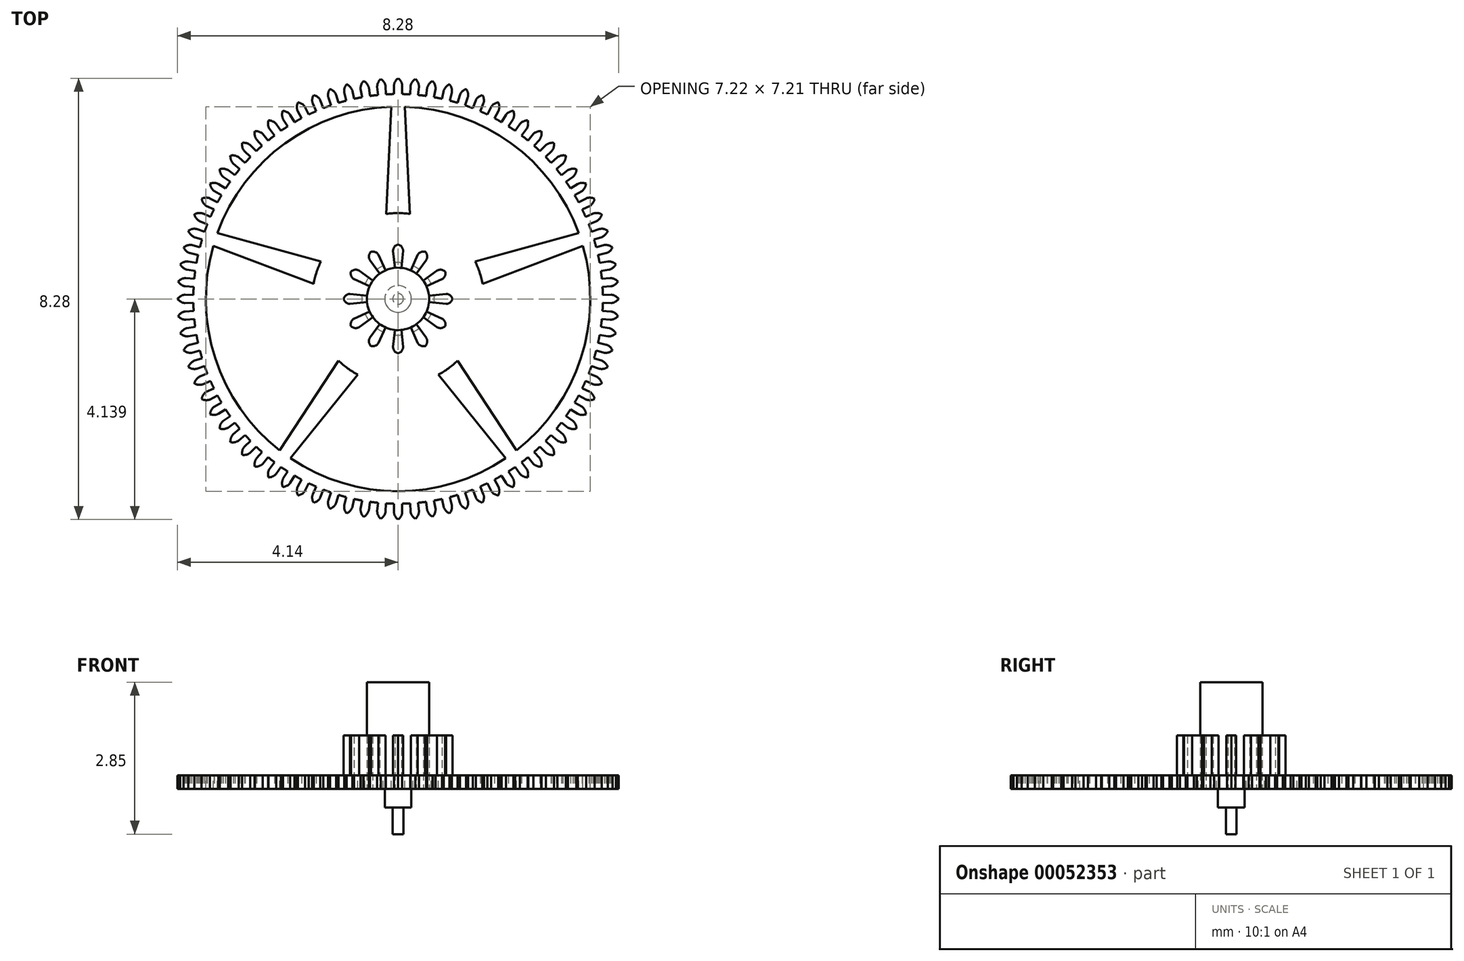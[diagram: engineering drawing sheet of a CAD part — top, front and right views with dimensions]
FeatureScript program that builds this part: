
annotation { "Feature Type Name" : "Feature", "Feature Type Description" : "" }
export const myFeature = defineFeature(function(context is Context, id is Id, definition is map)
    precondition{}
    {
        {
            var Q0;
            Q0=qCreatedBy(makeId("Top.planeOp"),FACE);
            var sketch = newSketch(context, id + "F0", { "sketchPlane" : qUnion([Q0])});
            skCircle(sketch, "E0", {"center": v(0, 0) * mm, "radius": 3.84 * mm});
            skCircle(sketch, "E1", {"center": v(0, 0) * mm, "radius": 4 * mm, "construction": true});
            skCircle(sketch, "E2", {"center": v(0, 0) * mm, "radius": 4.14 * mm, "construction": true});
            skLineSegment(sketch, "E3", {"start": v(0, 0) * mm, "end": v(0, 4) * mm, "construction": true});
            skLineSegment(sketch, "E4", {"start": v(0, 4) * mm, "end": v(0.08, 4) * mm, "construction": true});
            skLineSegment(sketch, "E5", {"start": v(0, 4) * mm, "end": v(-0.08, 4) * mm, "construction": true});
            skLineSegment(sketch, "E6", {"start": v(-0.08, 4) * mm, "end": v(0, 0) * mm, "construction": true});
            skLineSegment(sketch, "E7", {"start": v(0.08, 4) * mm, "end": v(0, 0) * mm, "construction": true});
            skLineSegment(sketch, "E8", {"start": v(-0.08, 4) * mm, "end": v(-0.08, 3.84) * mm});
            skLineSegment(sketch, "E9", {"start": v(0.08, 4) * mm, "end": v(0.08, 3.84) * mm});
            skCircle(sketch, "E10", {"center": v(-0.08, 4) * mm, "radius": 0.2 * mm, "construction": true});
            skCircle(sketch, "E11", {"center": v(0, 4.14) * mm, "radius": 0.2 * mm, "construction": true});
            skArc(sketch, "E12", {"start": v(-0.08, 4) * mm, "mid": v(-0.05, 4.08) * mm, "end": v(0, 4.14) * mm});
            skCircle(sketch, "E13", {"center": v(0.08, 4) * mm, "radius": 0.2 * mm, "construction": true});
            skArc(sketch, "E14", {"start": v(0.08, 4) * mm, "mid": v(0.05, 4.08) * mm, "end": v(0, 4.14) * mm});
            skSolve(sketch);
        }
        {
            var Q0;
            {var subQ2=sQuery(id+"F0.wireOp",EDGE,"E8");Q0=makeQuery(id+"F0.imprint","IMPRINT",FACE,{"disambiguationData":[TD([[makeQuery(id+"F0.imprint","IMPRINT",EDGE,{"derivedFrom":subQ2}),1.0]])]});}
            extrude(context, id + "F1", {"entities" : qUnion([Q0]), "depth" : 0.25 * mm});
        }
        {
            var Q0;
            Q0=makeQuery(id+"F1.opExtrude","SWEPT_BODY",BODY,{"disambiguationData":[OSD([sQuery(id+"F0.wireOp",EDGE,"E0"),sQuery(id+"F0.wireOp",EDGE,"E8"),sQuery(id+"F0.wireOp",EDGE,"E9"),sQuery(id+"F0.wireOp",EDGE,"E12"),sQuery(id+"F0.wireOp",EDGE,"E14")])]});
            var Q1;
            Q1=makeQuery(id+"F1.opExtrude","CAP_EDGE",EDGE,{"disambiguationData":[OSD([sQuery(id+"F0.wireOp",EDGE,"E0")])],"isStart":false});
            circularPattern(context, id + "F2", {"entities" : qUnion([Q0]), "axis" : qUnion([Q1]), "angle" : 4.5 * degree, "instanceCount" : round(80)});
        }
        {
            var Q0;
            {var subQ0=sQuery(id+"F0.wireOp",EDGE,"E0");var subQ2=makeQuery(id+"F0.imprint","INTERSECT",VERTEX,{"derivedFrom":[subQ0,sQuery(id+"F0.wireOp",EDGE,"E8")]});Q0=makeQuery(id+"F0.imprint","IMPRINT",FACE,{"disambiguationData":[TD([[makeQuery(id+"F0.imprint","IMPRINT",EDGE,{"disambiguationData":[TD([[subQ2,1.0]])],"derivedFrom":subQ0}),1.0]])]});}
            extrude(context, id + "F3", {"entities" : qUnion([Q0]), "depth" : 0.25 * mm});
        }
        {
            var Q0;
            Q0=makeQuery(id+"F2.opPattern","COPY",BODY,{"derivedFrom":makeQuery(id+"F1.opExtrude","SWEPT_BODY",BODY,{"disambiguationData":[OSD([sQuery(id+"F0.wireOp",EDGE,"E0"),sQuery(id+"F0.wireOp",EDGE,"E8"),sQuery(id+"F0.wireOp",EDGE,"E9"),sQuery(id+"F0.wireOp",EDGE,"E12"),sQuery(id+"F0.wireOp",EDGE,"E14")])]}),"instanceName":"94"});
            var Q1;
            Q1=makeQuery(id+"F2.opPattern","COPY",BODY,{"derivedFrom":makeQuery(id+"F1.opExtrude","SWEPT_BODY",BODY,{"disambiguationData":[OSD([sQuery(id+"F0.wireOp",EDGE,"E0"),sQuery(id+"F0.wireOp",EDGE,"E8"),sQuery(id+"F0.wireOp",EDGE,"E9"),sQuery(id+"F0.wireOp",EDGE,"E12"),sQuery(id+"F0.wireOp",EDGE,"E14")])]}),"instanceName":"73"});
            var Q2;
            Q2=makeQuery(id+"F2.opPattern","COPY",BODY,{"derivedFrom":makeQuery(id+"F1.opExtrude","SWEPT_BODY",BODY,{"disambiguationData":[OSD([sQuery(id+"F0.wireOp",EDGE,"E0"),sQuery(id+"F0.wireOp",EDGE,"E8"),sQuery(id+"F0.wireOp",EDGE,"E9"),sQuery(id+"F0.wireOp",EDGE,"E12"),sQuery(id+"F0.wireOp",EDGE,"E14")])]}),"instanceName":"71"});
            var Q3;
            Q3=makeQuery(id+"F2.opPattern","COPY",BODY,{"derivedFrom":makeQuery(id+"F1.opExtrude","SWEPT_BODY",BODY,{"disambiguationData":[OSD([sQuery(id+"F0.wireOp",EDGE,"E0"),sQuery(id+"F0.wireOp",EDGE,"E8"),sQuery(id+"F0.wireOp",EDGE,"E9"),sQuery(id+"F0.wireOp",EDGE,"E12"),sQuery(id+"F0.wireOp",EDGE,"E14")])]}),"instanceName":"78"});
            var Q4;
            Q4=makeQuery(id+"F2.opPattern","COPY",BODY,{"derivedFrom":makeQuery(id+"F1.opExtrude","SWEPT_BODY",BODY,{"disambiguationData":[OSD([sQuery(id+"F0.wireOp",EDGE,"E0"),sQuery(id+"F0.wireOp",EDGE,"E8"),sQuery(id+"F0.wireOp",EDGE,"E9"),sQuery(id+"F0.wireOp",EDGE,"E12"),sQuery(id+"F0.wireOp",EDGE,"E14")])]}),"instanceName":"82"});
            var Q5;
            Q5=makeQuery(id+"F2.opPattern","COPY",BODY,{"derivedFrom":makeQuery(id+"F1.opExtrude","SWEPT_BODY",BODY,{"disambiguationData":[OSD([sQuery(id+"F0.wireOp",EDGE,"E0"),sQuery(id+"F0.wireOp",EDGE,"E8"),sQuery(id+"F0.wireOp",EDGE,"E9"),sQuery(id+"F0.wireOp",EDGE,"E12"),sQuery(id+"F0.wireOp",EDGE,"E14")])]}),"instanceName":"90"});
            var Q6;
            Q6=makeQuery(id+"F2.opPattern","COPY",BODY,{"derivedFrom":makeQuery(id+"F1.opExtrude","SWEPT_BODY",BODY,{"disambiguationData":[OSD([sQuery(id+"F0.wireOp",EDGE,"E0"),sQuery(id+"F0.wireOp",EDGE,"E8"),sQuery(id+"F0.wireOp",EDGE,"E9"),sQuery(id+"F0.wireOp",EDGE,"E12"),sQuery(id+"F0.wireOp",EDGE,"E14")])]}),"instanceName":"77"});
            var Q7;
            Q7=makeQuery(id+"F2.opPattern","COPY",BODY,{"derivedFrom":makeQuery(id+"F1.opExtrude","SWEPT_BODY",BODY,{"disambiguationData":[OSD([sQuery(id+"F0.wireOp",EDGE,"E0"),sQuery(id+"F0.wireOp",EDGE,"E8"),sQuery(id+"F0.wireOp",EDGE,"E9"),sQuery(id+"F0.wireOp",EDGE,"E12"),sQuery(id+"F0.wireOp",EDGE,"E14")])]}),"instanceName":"76"});
            var Q8;
            Q8=makeQuery(id+"F2.opPattern","COPY",BODY,{"derivedFrom":makeQuery(id+"F1.opExtrude","SWEPT_BODY",BODY,{"disambiguationData":[OSD([sQuery(id+"F0.wireOp",EDGE,"E0"),sQuery(id+"F0.wireOp",EDGE,"E8"),sQuery(id+"F0.wireOp",EDGE,"E9"),sQuery(id+"F0.wireOp",EDGE,"E12"),sQuery(id+"F0.wireOp",EDGE,"E14")])]}),"instanceName":"84"});
            var Q9;
            Q9=makeQuery(id+"F2.opPattern","COPY",BODY,{"derivedFrom":makeQuery(id+"F1.opExtrude","SWEPT_BODY",BODY,{"disambiguationData":[OSD([sQuery(id+"F0.wireOp",EDGE,"E0"),sQuery(id+"F0.wireOp",EDGE,"E8"),sQuery(id+"F0.wireOp",EDGE,"E9"),sQuery(id+"F0.wireOp",EDGE,"E12"),sQuery(id+"F0.wireOp",EDGE,"E14")])]}),"instanceName":"80"});
            var Q10;
            Q10=makeQuery(id+"F2.opPattern","COPY",BODY,{"derivedFrom":makeQuery(id+"F1.opExtrude","SWEPT_BODY",BODY,{"disambiguationData":[OSD([sQuery(id+"F0.wireOp",EDGE,"E0"),sQuery(id+"F0.wireOp",EDGE,"E8"),sQuery(id+"F0.wireOp",EDGE,"E9"),sQuery(id+"F0.wireOp",EDGE,"E12"),sQuery(id+"F0.wireOp",EDGE,"E14")])]}),"instanceName":"37"});
            var Q11;
            Q11=makeQuery(id+"F2.opPattern","COPY",BODY,{"derivedFrom":makeQuery(id+"F1.opExtrude","SWEPT_BODY",BODY,{"disambiguationData":[OSD([sQuery(id+"F0.wireOp",EDGE,"E0"),sQuery(id+"F0.wireOp",EDGE,"E8"),sQuery(id+"F0.wireOp",EDGE,"E9"),sQuery(id+"F0.wireOp",EDGE,"E12"),sQuery(id+"F0.wireOp",EDGE,"E14")])]}),"instanceName":"44"});
            var Q12;
            Q12=makeQuery(id+"F2.opPattern","COPY",BODY,{"derivedFrom":makeQuery(id+"F1.opExtrude","SWEPT_BODY",BODY,{"disambiguationData":[OSD([sQuery(id+"F0.wireOp",EDGE,"E0"),sQuery(id+"F0.wireOp",EDGE,"E8"),sQuery(id+"F0.wireOp",EDGE,"E9"),sQuery(id+"F0.wireOp",EDGE,"E12"),sQuery(id+"F0.wireOp",EDGE,"E14")])]}),"instanceName":"88"});
            var Q13;
            Q13=makeQuery(id+"F2.opPattern","COPY",BODY,{"derivedFrom":makeQuery(id+"F1.opExtrude","SWEPT_BODY",BODY,{"disambiguationData":[OSD([sQuery(id+"F0.wireOp",EDGE,"E0"),sQuery(id+"F0.wireOp",EDGE,"E8"),sQuery(id+"F0.wireOp",EDGE,"E9"),sQuery(id+"F0.wireOp",EDGE,"E12"),sQuery(id+"F0.wireOp",EDGE,"E14")])]}),"instanceName":"60"});
            var Q14;
            Q14=makeQuery(id+"F2.opPattern","COPY",BODY,{"derivedFrom":makeQuery(id+"F1.opExtrude","SWEPT_BODY",BODY,{"disambiguationData":[OSD([sQuery(id+"F0.wireOp",EDGE,"E0"),sQuery(id+"F0.wireOp",EDGE,"E8"),sQuery(id+"F0.wireOp",EDGE,"E9"),sQuery(id+"F0.wireOp",EDGE,"E12"),sQuery(id+"F0.wireOp",EDGE,"E14")])]}),"instanceName":"69"});
            var Q15;
            Q15=makeQuery(id+"F2.opPattern","COPY",BODY,{"derivedFrom":makeQuery(id+"F1.opExtrude","SWEPT_BODY",BODY,{"disambiguationData":[OSD([sQuery(id+"F0.wireOp",EDGE,"E0"),sQuery(id+"F0.wireOp",EDGE,"E8"),sQuery(id+"F0.wireOp",EDGE,"E9"),sQuery(id+"F0.wireOp",EDGE,"E12"),sQuery(id+"F0.wireOp",EDGE,"E14")])]}),"instanceName":"12"});
            var Q16;
            Q16=makeQuery(id+"F2.opPattern","COPY",BODY,{"derivedFrom":makeQuery(id+"F1.opExtrude","SWEPT_BODY",BODY,{"disambiguationData":[OSD([sQuery(id+"F0.wireOp",EDGE,"E0"),sQuery(id+"F0.wireOp",EDGE,"E8"),sQuery(id+"F0.wireOp",EDGE,"E9"),sQuery(id+"F0.wireOp",EDGE,"E12"),sQuery(id+"F0.wireOp",EDGE,"E14")])]}),"instanceName":"28"});
            var Q17;
            Q17=makeQuery(id+"F2.opPattern","COPY",BODY,{"derivedFrom":makeQuery(id+"F1.opExtrude","SWEPT_BODY",BODY,{"disambiguationData":[OSD([sQuery(id+"F0.wireOp",EDGE,"E0"),sQuery(id+"F0.wireOp",EDGE,"E8"),sQuery(id+"F0.wireOp",EDGE,"E9"),sQuery(id+"F0.wireOp",EDGE,"E12"),sQuery(id+"F0.wireOp",EDGE,"E14")])]}),"instanceName":"92"});
            var Q18;
            Q18=makeQuery(id+"F2.opPattern","COPY",BODY,{"derivedFrom":makeQuery(id+"F1.opExtrude","SWEPT_BODY",BODY,{"disambiguationData":[OSD([sQuery(id+"F0.wireOp",EDGE,"E0"),sQuery(id+"F0.wireOp",EDGE,"E8"),sQuery(id+"F0.wireOp",EDGE,"E9"),sQuery(id+"F0.wireOp",EDGE,"E12"),sQuery(id+"F0.wireOp",EDGE,"E14")])]}),"instanceName":"89"});
            var Q19;
            Q19=makeQuery(id+"F2.opPattern","COPY",BODY,{"derivedFrom":makeQuery(id+"F1.opExtrude","SWEPT_BODY",BODY,{"disambiguationData":[OSD([sQuery(id+"F0.wireOp",EDGE,"E0"),sQuery(id+"F0.wireOp",EDGE,"E8"),sQuery(id+"F0.wireOp",EDGE,"E9"),sQuery(id+"F0.wireOp",EDGE,"E12"),sQuery(id+"F0.wireOp",EDGE,"E14")])]}),"instanceName":"7"});
            var Q20;
            Q20=makeQuery(id+"F2.opPattern","COPY",BODY,{"derivedFrom":makeQuery(id+"F1.opExtrude","SWEPT_BODY",BODY,{"disambiguationData":[OSD([sQuery(id+"F0.wireOp",EDGE,"E0"),sQuery(id+"F0.wireOp",EDGE,"E8"),sQuery(id+"F0.wireOp",EDGE,"E9"),sQuery(id+"F0.wireOp",EDGE,"E12"),sQuery(id+"F0.wireOp",EDGE,"E14")])]}),"instanceName":"14"});
            var Q21;
            Q21=makeQuery(id+"F2.opPattern","COPY",BODY,{"derivedFrom":makeQuery(id+"F1.opExtrude","SWEPT_BODY",BODY,{"disambiguationData":[OSD([sQuery(id+"F0.wireOp",EDGE,"E0"),sQuery(id+"F0.wireOp",EDGE,"E8"),sQuery(id+"F0.wireOp",EDGE,"E9"),sQuery(id+"F0.wireOp",EDGE,"E12"),sQuery(id+"F0.wireOp",EDGE,"E14")])]}),"instanceName":"32"});
            var Q22;
            Q22=makeQuery(id+"F2.opPattern","COPY",BODY,{"derivedFrom":makeQuery(id+"F1.opExtrude","SWEPT_BODY",BODY,{"disambiguationData":[OSD([sQuery(id+"F0.wireOp",EDGE,"E0"),sQuery(id+"F0.wireOp",EDGE,"E8"),sQuery(id+"F0.wireOp",EDGE,"E9"),sQuery(id+"F0.wireOp",EDGE,"E12"),sQuery(id+"F0.wireOp",EDGE,"E14")])]}),"instanceName":"25"});
            var Q23;
            Q23=makeQuery(id+"F2.opPattern","COPY",BODY,{"derivedFrom":makeQuery(id+"F1.opExtrude","SWEPT_BODY",BODY,{"disambiguationData":[OSD([sQuery(id+"F0.wireOp",EDGE,"E0"),sQuery(id+"F0.wireOp",EDGE,"E8"),sQuery(id+"F0.wireOp",EDGE,"E9"),sQuery(id+"F0.wireOp",EDGE,"E12"),sQuery(id+"F0.wireOp",EDGE,"E14")])]}),"instanceName":"34"});
            var Q24;
            Q24=makeQuery(id+"F2.opPattern","COPY",BODY,{"derivedFrom":makeQuery(id+"F1.opExtrude","SWEPT_BODY",BODY,{"disambiguationData":[OSD([sQuery(id+"F0.wireOp",EDGE,"E0"),sQuery(id+"F0.wireOp",EDGE,"E8"),sQuery(id+"F0.wireOp",EDGE,"E9"),sQuery(id+"F0.wireOp",EDGE,"E12"),sQuery(id+"F0.wireOp",EDGE,"E14")])]}),"instanceName":"30"});
            var Q25;
            Q25=makeQuery(id+"F2.opPattern","COPY",BODY,{"derivedFrom":makeQuery(id+"F1.opExtrude","SWEPT_BODY",BODY,{"disambiguationData":[OSD([sQuery(id+"F0.wireOp",EDGE,"E0"),sQuery(id+"F0.wireOp",EDGE,"E8"),sQuery(id+"F0.wireOp",EDGE,"E9"),sQuery(id+"F0.wireOp",EDGE,"E12"),sQuery(id+"F0.wireOp",EDGE,"E14")])]}),"instanceName":"66"});
            var Q26;
            Q26=makeQuery(id+"F2.opPattern","COPY",BODY,{"derivedFrom":makeQuery(id+"F1.opExtrude","SWEPT_BODY",BODY,{"disambiguationData":[OSD([sQuery(id+"F0.wireOp",EDGE,"E0"),sQuery(id+"F0.wireOp",EDGE,"E8"),sQuery(id+"F0.wireOp",EDGE,"E9"),sQuery(id+"F0.wireOp",EDGE,"E12"),sQuery(id+"F0.wireOp",EDGE,"E14")])]}),"instanceName":"18"});
            var Q27;
            Q27=makeQuery(id+"F2.opPattern","COPY",BODY,{"derivedFrom":makeQuery(id+"F1.opExtrude","SWEPT_BODY",BODY,{"disambiguationData":[OSD([sQuery(id+"F0.wireOp",EDGE,"E0"),sQuery(id+"F0.wireOp",EDGE,"E8"),sQuery(id+"F0.wireOp",EDGE,"E9"),sQuery(id+"F0.wireOp",EDGE,"E12"),sQuery(id+"F0.wireOp",EDGE,"E14")])]}),"instanceName":"59"});
            var Q28;
            Q28=makeQuery(id+"F2.opPattern","COPY",BODY,{"derivedFrom":makeQuery(id+"F1.opExtrude","SWEPT_BODY",BODY,{"disambiguationData":[OSD([sQuery(id+"F0.wireOp",EDGE,"E0"),sQuery(id+"F0.wireOp",EDGE,"E8"),sQuery(id+"F0.wireOp",EDGE,"E9"),sQuery(id+"F0.wireOp",EDGE,"E12"),sQuery(id+"F0.wireOp",EDGE,"E14")])]}),"instanceName":"50"});
            var Q29;
            Q29=makeQuery(id+"F2.opPattern","COPY",BODY,{"derivedFrom":makeQuery(id+"F1.opExtrude","SWEPT_BODY",BODY,{"disambiguationData":[OSD([sQuery(id+"F0.wireOp",EDGE,"E0"),sQuery(id+"F0.wireOp",EDGE,"E8"),sQuery(id+"F0.wireOp",EDGE,"E9"),sQuery(id+"F0.wireOp",EDGE,"E12"),sQuery(id+"F0.wireOp",EDGE,"E14")])]}),"instanceName":"46"});
            var Q30;
            Q30=makeQuery(id+"F2.opPattern","COPY",BODY,{"derivedFrom":makeQuery(id+"F1.opExtrude","SWEPT_BODY",BODY,{"disambiguationData":[OSD([sQuery(id+"F0.wireOp",EDGE,"E0"),sQuery(id+"F0.wireOp",EDGE,"E8"),sQuery(id+"F0.wireOp",EDGE,"E9"),sQuery(id+"F0.wireOp",EDGE,"E12"),sQuery(id+"F0.wireOp",EDGE,"E14")])]}),"instanceName":"57"});
            var Q31;
            Q31=makeQuery(id+"F2.opPattern","COPY",BODY,{"derivedFrom":makeQuery(id+"F1.opExtrude","SWEPT_BODY",BODY,{"disambiguationData":[OSD([sQuery(id+"F0.wireOp",EDGE,"E0"),sQuery(id+"F0.wireOp",EDGE,"E8"),sQuery(id+"F0.wireOp",EDGE,"E9"),sQuery(id+"F0.wireOp",EDGE,"E12"),sQuery(id+"F0.wireOp",EDGE,"E14")])]}),"instanceName":"64"});
            var Q32;
            Q32=makeQuery(id+"F2.opPattern","COPY",BODY,{"derivedFrom":makeQuery(id+"F1.opExtrude","SWEPT_BODY",BODY,{"disambiguationData":[OSD([sQuery(id+"F0.wireOp",EDGE,"E0"),sQuery(id+"F0.wireOp",EDGE,"E8"),sQuery(id+"F0.wireOp",EDGE,"E9"),sQuery(id+"F0.wireOp",EDGE,"E12"),sQuery(id+"F0.wireOp",EDGE,"E14")])]}),"instanceName":"62"});
            var Q33;
            Q33=makeQuery(id+"F2.opPattern","COPY",BODY,{"derivedFrom":makeQuery(id+"F1.opExtrude","SWEPT_BODY",BODY,{"disambiguationData":[OSD([sQuery(id+"F0.wireOp",EDGE,"E0"),sQuery(id+"F0.wireOp",EDGE,"E8"),sQuery(id+"F0.wireOp",EDGE,"E9"),sQuery(id+"F0.wireOp",EDGE,"E12"),sQuery(id+"F0.wireOp",EDGE,"E14")])]}),"instanceName":"5"});
            var Q34;
            Q34=makeQuery(id+"F2.opPattern","COPY",BODY,{"derivedFrom":makeQuery(id+"F1.opExtrude","SWEPT_BODY",BODY,{"disambiguationData":[OSD([sQuery(id+"F0.wireOp",EDGE,"E0"),sQuery(id+"F0.wireOp",EDGE,"E8"),sQuery(id+"F0.wireOp",EDGE,"E9"),sQuery(id+"F0.wireOp",EDGE,"E12"),sQuery(id+"F0.wireOp",EDGE,"E14")])]}),"instanceName":"16"});
            var Q35;
            Q35=makeQuery(id+"F2.opPattern","COPY",BODY,{"derivedFrom":makeQuery(id+"F1.opExtrude","SWEPT_BODY",BODY,{"disambiguationData":[OSD([sQuery(id+"F0.wireOp",EDGE,"E0"),sQuery(id+"F0.wireOp",EDGE,"E8"),sQuery(id+"F0.wireOp",EDGE,"E9"),sQuery(id+"F0.wireOp",EDGE,"E12"),sQuery(id+"F0.wireOp",EDGE,"E14")])]}),"instanceName":"31"});
            var Q36;
            Q36=makeQuery(id+"F2.opPattern","COPY",BODY,{"derivedFrom":makeQuery(id+"F1.opExtrude","SWEPT_BODY",BODY,{"disambiguationData":[OSD([sQuery(id+"F0.wireOp",EDGE,"E0"),sQuery(id+"F0.wireOp",EDGE,"E8"),sQuery(id+"F0.wireOp",EDGE,"E9"),sQuery(id+"F0.wireOp",EDGE,"E12"),sQuery(id+"F0.wireOp",EDGE,"E14")])]}),"instanceName":"21"});
            var Q37;
            Q37=makeQuery(id+"F2.opPattern","COPY",BODY,{"derivedFrom":makeQuery(id+"F1.opExtrude","SWEPT_BODY",BODY,{"disambiguationData":[OSD([sQuery(id+"F0.wireOp",EDGE,"E0"),sQuery(id+"F0.wireOp",EDGE,"E8"),sQuery(id+"F0.wireOp",EDGE,"E9"),sQuery(id+"F0.wireOp",EDGE,"E12"),sQuery(id+"F0.wireOp",EDGE,"E14")])]}),"instanceName":"43"});
            var Q38;
            Q38=makeQuery(id+"F2.opPattern","COPY",BODY,{"derivedFrom":makeQuery(id+"F1.opExtrude","SWEPT_BODY",BODY,{"disambiguationData":[OSD([sQuery(id+"F0.wireOp",EDGE,"E0"),sQuery(id+"F0.wireOp",EDGE,"E8"),sQuery(id+"F0.wireOp",EDGE,"E9"),sQuery(id+"F0.wireOp",EDGE,"E12"),sQuery(id+"F0.wireOp",EDGE,"E14")])]}),"instanceName":"53"});
            var Q39;
            Q39=makeQuery(id+"F2.opPattern","COPY",BODY,{"derivedFrom":makeQuery(id+"F1.opExtrude","SWEPT_BODY",BODY,{"disambiguationData":[OSD([sQuery(id+"F0.wireOp",EDGE,"E0"),sQuery(id+"F0.wireOp",EDGE,"E8"),sQuery(id+"F0.wireOp",EDGE,"E9"),sQuery(id+"F0.wireOp",EDGE,"E12"),sQuery(id+"F0.wireOp",EDGE,"E14")])]}),"instanceName":"49"});
            var Q40;
            Q40=makeQuery(id+"F2.opPattern","COPY",BODY,{"derivedFrom":makeQuery(id+"F1.opExtrude","SWEPT_BODY",BODY,{"disambiguationData":[OSD([sQuery(id+"F0.wireOp",EDGE,"E0"),sQuery(id+"F0.wireOp",EDGE,"E8"),sQuery(id+"F0.wireOp",EDGE,"E9"),sQuery(id+"F0.wireOp",EDGE,"E12"),sQuery(id+"F0.wireOp",EDGE,"E14")])]}),"instanceName":"65"});
            var Q41;
            Q41=makeQuery(id+"F2.opPattern","COPY",BODY,{"derivedFrom":makeQuery(id+"F1.opExtrude","SWEPT_BODY",BODY,{"disambiguationData":[OSD([sQuery(id+"F0.wireOp",EDGE,"E0"),sQuery(id+"F0.wireOp",EDGE,"E8"),sQuery(id+"F0.wireOp",EDGE,"E9"),sQuery(id+"F0.wireOp",EDGE,"E12"),sQuery(id+"F0.wireOp",EDGE,"E14")])]}),"instanceName":"74"});
            var Q42;
            Q42=makeQuery(id+"F2.opPattern","COPY",BODY,{"derivedFrom":makeQuery(id+"F1.opExtrude","SWEPT_BODY",BODY,{"disambiguationData":[OSD([sQuery(id+"F0.wireOp",EDGE,"E0"),sQuery(id+"F0.wireOp",EDGE,"E8"),sQuery(id+"F0.wireOp",EDGE,"E9"),sQuery(id+"F0.wireOp",EDGE,"E12"),sQuery(id+"F0.wireOp",EDGE,"E14")])]}),"instanceName":"17"});
            var Q43;
            Q43=makeQuery(id+"F2.opPattern","COPY",BODY,{"derivedFrom":makeQuery(id+"F1.opExtrude","SWEPT_BODY",BODY,{"disambiguationData":[OSD([sQuery(id+"F0.wireOp",EDGE,"E0"),sQuery(id+"F0.wireOp",EDGE,"E8"),sQuery(id+"F0.wireOp",EDGE,"E9"),sQuery(id+"F0.wireOp",EDGE,"E12"),sQuery(id+"F0.wireOp",EDGE,"E14")])]}),"instanceName":"58"});
            var Q44;
            Q44=makeQuery(id+"F2.opPattern","COPY",BODY,{"derivedFrom":makeQuery(id+"F1.opExtrude","SWEPT_BODY",BODY,{"disambiguationData":[OSD([sQuery(id+"F0.wireOp",EDGE,"E0"),sQuery(id+"F0.wireOp",EDGE,"E8"),sQuery(id+"F0.wireOp",EDGE,"E9"),sQuery(id+"F0.wireOp",EDGE,"E12"),sQuery(id+"F0.wireOp",EDGE,"E14")])]}),"instanceName":"85"});
            var Q45;
            Q45=makeQuery(id+"F2.opPattern","COPY",BODY,{"derivedFrom":makeQuery(id+"F1.opExtrude","SWEPT_BODY",BODY,{"disambiguationData":[OSD([sQuery(id+"F0.wireOp",EDGE,"E0"),sQuery(id+"F0.wireOp",EDGE,"E8"),sQuery(id+"F0.wireOp",EDGE,"E9"),sQuery(id+"F0.wireOp",EDGE,"E12"),sQuery(id+"F0.wireOp",EDGE,"E14")])]}),"instanceName":"81"});
            var Q46;
            Q46=makeQuery(id+"F2.opPattern","COPY",BODY,{"derivedFrom":makeQuery(id+"F1.opExtrude","SWEPT_BODY",BODY,{"disambiguationData":[OSD([sQuery(id+"F0.wireOp",EDGE,"E0"),sQuery(id+"F0.wireOp",EDGE,"E8"),sQuery(id+"F0.wireOp",EDGE,"E9"),sQuery(id+"F0.wireOp",EDGE,"E12"),sQuery(id+"F0.wireOp",EDGE,"E14")])]}),"instanceName":"42"});
            var Q47;
            Q47=makeQuery(id+"F2.opPattern","COPY",BODY,{"derivedFrom":makeQuery(id+"F1.opExtrude","SWEPT_BODY",BODY,{"disambiguationData":[OSD([sQuery(id+"F0.wireOp",EDGE,"E0"),sQuery(id+"F0.wireOp",EDGE,"E8"),sQuery(id+"F0.wireOp",EDGE,"E9"),sQuery(id+"F0.wireOp",EDGE,"E12"),sQuery(id+"F0.wireOp",EDGE,"E14")])]}),"instanceName":"10"});
            var Q48;
            Q48=makeQuery(id+"F2.opPattern","COPY",BODY,{"derivedFrom":makeQuery(id+"F1.opExtrude","SWEPT_BODY",BODY,{"disambiguationData":[OSD([sQuery(id+"F0.wireOp",EDGE,"E0"),sQuery(id+"F0.wireOp",EDGE,"E8"),sQuery(id+"F0.wireOp",EDGE,"E9"),sQuery(id+"F0.wireOp",EDGE,"E12"),sQuery(id+"F0.wireOp",EDGE,"E14")])]}),"instanceName":"79"});
            var Q49;
            Q49=makeQuery(id+"F2.opPattern","COPY",BODY,{"derivedFrom":makeQuery(id+"F1.opExtrude","SWEPT_BODY",BODY,{"disambiguationData":[OSD([sQuery(id+"F0.wireOp",EDGE,"E0"),sQuery(id+"F0.wireOp",EDGE,"E8"),sQuery(id+"F0.wireOp",EDGE,"E9"),sQuery(id+"F0.wireOp",EDGE,"E12"),sQuery(id+"F0.wireOp",EDGE,"E14")])]}),"instanceName":"83"});
            var Q50;
            Q50=makeQuery(id+"F2.opPattern","COPY",BODY,{"derivedFrom":makeQuery(id+"F1.opExtrude","SWEPT_BODY",BODY,{"disambiguationData":[OSD([sQuery(id+"F0.wireOp",EDGE,"E0"),sQuery(id+"F0.wireOp",EDGE,"E8"),sQuery(id+"F0.wireOp",EDGE,"E9"),sQuery(id+"F0.wireOp",EDGE,"E12"),sQuery(id+"F0.wireOp",EDGE,"E14")])]}),"instanceName":"13"});
            var Q51;
            Q51=makeQuery(id+"F2.opPattern","COPY",BODY,{"derivedFrom":makeQuery(id+"F1.opExtrude","SWEPT_BODY",BODY,{"disambiguationData":[OSD([sQuery(id+"F0.wireOp",EDGE,"E0"),sQuery(id+"F0.wireOp",EDGE,"E8"),sQuery(id+"F0.wireOp",EDGE,"E9"),sQuery(id+"F0.wireOp",EDGE,"E12"),sQuery(id+"F0.wireOp",EDGE,"E14")])]}),"instanceName":"86"});
            var Q52;
            Q52=makeQuery(id+"F2.opPattern","COPY",BODY,{"derivedFrom":makeQuery(id+"F1.opExtrude","SWEPT_BODY",BODY,{"disambiguationData":[OSD([sQuery(id+"F0.wireOp",EDGE,"E0"),sQuery(id+"F0.wireOp",EDGE,"E8"),sQuery(id+"F0.wireOp",EDGE,"E9"),sQuery(id+"F0.wireOp",EDGE,"E12"),sQuery(id+"F0.wireOp",EDGE,"E14")])]}),"instanceName":"3"});
            var Q53;
            Q53=makeQuery(id+"F2.opPattern","COPY",BODY,{"derivedFrom":makeQuery(id+"F1.opExtrude","SWEPT_BODY",BODY,{"disambiguationData":[OSD([sQuery(id+"F0.wireOp",EDGE,"E0"),sQuery(id+"F0.wireOp",EDGE,"E8"),sQuery(id+"F0.wireOp",EDGE,"E9"),sQuery(id+"F0.wireOp",EDGE,"E12"),sQuery(id+"F0.wireOp",EDGE,"E14")])]}),"instanceName":"70"});
            var Q54;
            Q54=makeQuery(id+"F2.opPattern","COPY",BODY,{"derivedFrom":makeQuery(id+"F1.opExtrude","SWEPT_BODY",BODY,{"disambiguationData":[OSD([sQuery(id+"F0.wireOp",EDGE,"E0"),sQuery(id+"F0.wireOp",EDGE,"E8"),sQuery(id+"F0.wireOp",EDGE,"E9"),sQuery(id+"F0.wireOp",EDGE,"E12"),sQuery(id+"F0.wireOp",EDGE,"E14")])]}),"instanceName":"61"});
            var Q55;
            Q55=makeQuery(id+"F2.opPattern","COPY",BODY,{"derivedFrom":makeQuery(id+"F1.opExtrude","SWEPT_BODY",BODY,{"disambiguationData":[OSD([sQuery(id+"F0.wireOp",EDGE,"E0"),sQuery(id+"F0.wireOp",EDGE,"E8"),sQuery(id+"F0.wireOp",EDGE,"E9"),sQuery(id+"F0.wireOp",EDGE,"E12"),sQuery(id+"F0.wireOp",EDGE,"E14")])]}),"instanceName":"87"});
            var Q56;
            Q56=makeQuery(id+"F2.opPattern","COPY",BODY,{"derivedFrom":makeQuery(id+"F1.opExtrude","SWEPT_BODY",BODY,{"disambiguationData":[OSD([sQuery(id+"F0.wireOp",EDGE,"E0"),sQuery(id+"F0.wireOp",EDGE,"E8"),sQuery(id+"F0.wireOp",EDGE,"E9"),sQuery(id+"F0.wireOp",EDGE,"E12"),sQuery(id+"F0.wireOp",EDGE,"E14")])]}),"instanceName":"35"});
            var Q57;
            Q57=makeQuery(id+"F2.opPattern","COPY",BODY,{"derivedFrom":makeQuery(id+"F1.opExtrude","SWEPT_BODY",BODY,{"disambiguationData":[OSD([sQuery(id+"F0.wireOp",EDGE,"E0"),sQuery(id+"F0.wireOp",EDGE,"E8"),sQuery(id+"F0.wireOp",EDGE,"E9"),sQuery(id+"F0.wireOp",EDGE,"E12"),sQuery(id+"F0.wireOp",EDGE,"E14")])]}),"instanceName":"47"});
            var Q58;
            Q58=makeQuery(id+"F2.opPattern","COPY",BODY,{"derivedFrom":makeQuery(id+"F1.opExtrude","SWEPT_BODY",BODY,{"disambiguationData":[OSD([sQuery(id+"F0.wireOp",EDGE,"E0"),sQuery(id+"F0.wireOp",EDGE,"E8"),sQuery(id+"F0.wireOp",EDGE,"E9"),sQuery(id+"F0.wireOp",EDGE,"E12"),sQuery(id+"F0.wireOp",EDGE,"E14")])]}),"instanceName":"39"});
            var Q59;
            Q59=makeQuery(id+"F2.opPattern","COPY",BODY,{"derivedFrom":makeQuery(id+"F1.opExtrude","SWEPT_BODY",BODY,{"disambiguationData":[OSD([sQuery(id+"F0.wireOp",EDGE,"E0"),sQuery(id+"F0.wireOp",EDGE,"E8"),sQuery(id+"F0.wireOp",EDGE,"E9"),sQuery(id+"F0.wireOp",EDGE,"E12"),sQuery(id+"F0.wireOp",EDGE,"E14")])]}),"instanceName":"51"});
            var Q60;
            Q60=makeQuery(id+"F2.opPattern","COPY",BODY,{"derivedFrom":makeQuery(id+"F1.opExtrude","SWEPT_BODY",BODY,{"disambiguationData":[OSD([sQuery(id+"F0.wireOp",EDGE,"E0"),sQuery(id+"F0.wireOp",EDGE,"E8"),sQuery(id+"F0.wireOp",EDGE,"E9"),sQuery(id+"F0.wireOp",EDGE,"E12"),sQuery(id+"F0.wireOp",EDGE,"E14")])]}),"instanceName":"67"});
            var Q61;
            Q61=makeQuery(id+"F2.opPattern","COPY",BODY,{"derivedFrom":makeQuery(id+"F1.opExtrude","SWEPT_BODY",BODY,{"disambiguationData":[OSD([sQuery(id+"F0.wireOp",EDGE,"E0"),sQuery(id+"F0.wireOp",EDGE,"E8"),sQuery(id+"F0.wireOp",EDGE,"E9"),sQuery(id+"F0.wireOp",EDGE,"E12"),sQuery(id+"F0.wireOp",EDGE,"E14")])]}),"instanceName":"26"});
            var Q62;
            Q62=makeQuery(id+"F2.opPattern","COPY",BODY,{"derivedFrom":makeQuery(id+"F1.opExtrude","SWEPT_BODY",BODY,{"disambiguationData":[OSD([sQuery(id+"F0.wireOp",EDGE,"E0"),sQuery(id+"F0.wireOp",EDGE,"E8"),sQuery(id+"F0.wireOp",EDGE,"E9"),sQuery(id+"F0.wireOp",EDGE,"E12"),sQuery(id+"F0.wireOp",EDGE,"E14")])]}),"instanceName":"19"});
            var Q63;
            Q63=makeQuery(id+"F2.opPattern","COPY",BODY,{"derivedFrom":makeQuery(id+"F1.opExtrude","SWEPT_BODY",BODY,{"disambiguationData":[OSD([sQuery(id+"F0.wireOp",EDGE,"E0"),sQuery(id+"F0.wireOp",EDGE,"E8"),sQuery(id+"F0.wireOp",EDGE,"E9"),sQuery(id+"F0.wireOp",EDGE,"E12"),sQuery(id+"F0.wireOp",EDGE,"E14")])]}),"instanceName":"23"});
            var Q64;
            Q64=makeQuery(id+"F2.opPattern","COPY",BODY,{"derivedFrom":makeQuery(id+"F1.opExtrude","SWEPT_BODY",BODY,{"disambiguationData":[OSD([sQuery(id+"F0.wireOp",EDGE,"E0"),sQuery(id+"F0.wireOp",EDGE,"E8"),sQuery(id+"F0.wireOp",EDGE,"E9"),sQuery(id+"F0.wireOp",EDGE,"E12"),sQuery(id+"F0.wireOp",EDGE,"E14")])]}),"instanceName":"27"});
            var Q65;
            Q65=makeQuery(id+"F2.opPattern","COPY",BODY,{"derivedFrom":makeQuery(id+"F1.opExtrude","SWEPT_BODY",BODY,{"disambiguationData":[OSD([sQuery(id+"F0.wireOp",EDGE,"E0"),sQuery(id+"F0.wireOp",EDGE,"E8"),sQuery(id+"F0.wireOp",EDGE,"E9"),sQuery(id+"F0.wireOp",EDGE,"E12"),sQuery(id+"F0.wireOp",EDGE,"E14")])]}),"instanceName":"29"});
            var Q66;
            Q66=makeQuery(id+"F2.opPattern","COPY",BODY,{"derivedFrom":makeQuery(id+"F1.opExtrude","SWEPT_BODY",BODY,{"disambiguationData":[OSD([sQuery(id+"F0.wireOp",EDGE,"E0"),sQuery(id+"F0.wireOp",EDGE,"E8"),sQuery(id+"F0.wireOp",EDGE,"E9"),sQuery(id+"F0.wireOp",EDGE,"E12"),sQuery(id+"F0.wireOp",EDGE,"E14")])]}),"instanceName":"11"});
            var Q67;
            Q67=makeQuery(id+"F2.opPattern","COPY",BODY,{"derivedFrom":makeQuery(id+"F1.opExtrude","SWEPT_BODY",BODY,{"disambiguationData":[OSD([sQuery(id+"F0.wireOp",EDGE,"E0"),sQuery(id+"F0.wireOp",EDGE,"E8"),sQuery(id+"F0.wireOp",EDGE,"E9"),sQuery(id+"F0.wireOp",EDGE,"E12"),sQuery(id+"F0.wireOp",EDGE,"E14")])]}),"instanceName":"33"});
            var Q68;
            Q68=makeQuery(id+"F2.opPattern","COPY",BODY,{"derivedFrom":makeQuery(id+"F1.opExtrude","SWEPT_BODY",BODY,{"disambiguationData":[OSD([sQuery(id+"F0.wireOp",EDGE,"E0"),sQuery(id+"F0.wireOp",EDGE,"E8"),sQuery(id+"F0.wireOp",EDGE,"E9"),sQuery(id+"F0.wireOp",EDGE,"E12"),sQuery(id+"F0.wireOp",EDGE,"E14")])]}),"instanceName":"41"});
            var Q69;
            Q69=makeQuery(id+"F2.opPattern","COPY",BODY,{"derivedFrom":makeQuery(id+"F1.opExtrude","SWEPT_BODY",BODY,{"disambiguationData":[OSD([sQuery(id+"F0.wireOp",EDGE,"E0"),sQuery(id+"F0.wireOp",EDGE,"E8"),sQuery(id+"F0.wireOp",EDGE,"E9"),sQuery(id+"F0.wireOp",EDGE,"E12"),sQuery(id+"F0.wireOp",EDGE,"E14")])]}),"instanceName":"24"});
            var Q70;
            Q70=makeQuery(id+"F2.opPattern","COPY",BODY,{"derivedFrom":makeQuery(id+"F1.opExtrude","SWEPT_BODY",BODY,{"disambiguationData":[OSD([sQuery(id+"F0.wireOp",EDGE,"E0"),sQuery(id+"F0.wireOp",EDGE,"E8"),sQuery(id+"F0.wireOp",EDGE,"E9"),sQuery(id+"F0.wireOp",EDGE,"E12"),sQuery(id+"F0.wireOp",EDGE,"E14")])]}),"instanceName":"22"});
            var Q71;
            Q71=makeQuery(id+"F2.opPattern","COPY",BODY,{"derivedFrom":makeQuery(id+"F1.opExtrude","SWEPT_BODY",BODY,{"disambiguationData":[OSD([sQuery(id+"F0.wireOp",EDGE,"E0"),sQuery(id+"F0.wireOp",EDGE,"E8"),sQuery(id+"F0.wireOp",EDGE,"E9"),sQuery(id+"F0.wireOp",EDGE,"E12"),sQuery(id+"F0.wireOp",EDGE,"E14")])]}),"instanceName":"8"});
            var Q72;
            Q72=makeQuery(id+"F2.opPattern","COPY",BODY,{"derivedFrom":makeQuery(id+"F1.opExtrude","SWEPT_BODY",BODY,{"disambiguationData":[OSD([sQuery(id+"F0.wireOp",EDGE,"E0"),sQuery(id+"F0.wireOp",EDGE,"E8"),sQuery(id+"F0.wireOp",EDGE,"E9"),sQuery(id+"F0.wireOp",EDGE,"E12"),sQuery(id+"F0.wireOp",EDGE,"E14")])]}),"instanceName":"40"});
            var Q73;
            Q73=makeQuery(id+"F2.opPattern","COPY",BODY,{"derivedFrom":makeQuery(id+"F1.opExtrude","SWEPT_BODY",BODY,{"disambiguationData":[OSD([sQuery(id+"F0.wireOp",EDGE,"E0"),sQuery(id+"F0.wireOp",EDGE,"E8"),sQuery(id+"F0.wireOp",EDGE,"E9"),sQuery(id+"F0.wireOp",EDGE,"E12"),sQuery(id+"F0.wireOp",EDGE,"E14")])]}),"instanceName":"54"});
            var Q74;
            Q74=makeQuery(id+"F2.opPattern","COPY",BODY,{"derivedFrom":makeQuery(id+"F1.opExtrude","SWEPT_BODY",BODY,{"disambiguationData":[OSD([sQuery(id+"F0.wireOp",EDGE,"E0"),sQuery(id+"F0.wireOp",EDGE,"E8"),sQuery(id+"F0.wireOp",EDGE,"E9"),sQuery(id+"F0.wireOp",EDGE,"E12"),sQuery(id+"F0.wireOp",EDGE,"E14")])]}),"instanceName":"56"});
            var Q75;
            Q75=makeQuery(id+"F2.opPattern","COPY",BODY,{"derivedFrom":makeQuery(id+"F1.opExtrude","SWEPT_BODY",BODY,{"disambiguationData":[OSD([sQuery(id+"F0.wireOp",EDGE,"E0"),sQuery(id+"F0.wireOp",EDGE,"E8"),sQuery(id+"F0.wireOp",EDGE,"E9"),sQuery(id+"F0.wireOp",EDGE,"E12"),sQuery(id+"F0.wireOp",EDGE,"E14")])]}),"instanceName":"72"});
            var Q76;
            Q76=makeQuery(id+"F2.opPattern","COPY",BODY,{"derivedFrom":makeQuery(id+"F1.opExtrude","SWEPT_BODY",BODY,{"disambiguationData":[OSD([sQuery(id+"F0.wireOp",EDGE,"E0"),sQuery(id+"F0.wireOp",EDGE,"E8"),sQuery(id+"F0.wireOp",EDGE,"E9"),sQuery(id+"F0.wireOp",EDGE,"E12"),sQuery(id+"F0.wireOp",EDGE,"E14")])]}),"instanceName":"15"});
            var Q77;
            Q77=makeQuery(id+"F2.opPattern","COPY",BODY,{"derivedFrom":makeQuery(id+"F1.opExtrude","SWEPT_BODY",BODY,{"disambiguationData":[OSD([sQuery(id+"F0.wireOp",EDGE,"E0"),sQuery(id+"F0.wireOp",EDGE,"E8"),sQuery(id+"F0.wireOp",EDGE,"E9"),sQuery(id+"F0.wireOp",EDGE,"E12"),sQuery(id+"F0.wireOp",EDGE,"E14")])]}),"instanceName":"63"});
            var Q78;
            Q78=makeQuery(id+"F2.opPattern","COPY",BODY,{"derivedFrom":makeQuery(id+"F1.opExtrude","SWEPT_BODY",BODY,{"disambiguationData":[OSD([sQuery(id+"F0.wireOp",EDGE,"E0"),sQuery(id+"F0.wireOp",EDGE,"E8"),sQuery(id+"F0.wireOp",EDGE,"E9"),sQuery(id+"F0.wireOp",EDGE,"E12"),sQuery(id+"F0.wireOp",EDGE,"E14")])]}),"instanceName":"95"});
            var Q79;
            Q79=makeQuery(id+"F2.opPattern","COPY",BODY,{"derivedFrom":makeQuery(id+"F1.opExtrude","SWEPT_BODY",BODY,{"disambiguationData":[OSD([sQuery(id+"F0.wireOp",EDGE,"E0"),sQuery(id+"F0.wireOp",EDGE,"E8"),sQuery(id+"F0.wireOp",EDGE,"E9"),sQuery(id+"F0.wireOp",EDGE,"E12"),sQuery(id+"F0.wireOp",EDGE,"E14")])]}),"instanceName":"6"});
            var Q80;
            Q80=makeQuery(id+"F2.opPattern","COPY",BODY,{"derivedFrom":makeQuery(id+"F1.opExtrude","SWEPT_BODY",BODY,{"disambiguationData":[OSD([sQuery(id+"F0.wireOp",EDGE,"E0"),sQuery(id+"F0.wireOp",EDGE,"E8"),sQuery(id+"F0.wireOp",EDGE,"E9"),sQuery(id+"F0.wireOp",EDGE,"E12"),sQuery(id+"F0.wireOp",EDGE,"E14")])]}),"instanceName":"38"});
            var Q81;
            Q81=makeQuery(id+"F2.opPattern","COPY",BODY,{"derivedFrom":makeQuery(id+"F1.opExtrude","SWEPT_BODY",BODY,{"disambiguationData":[OSD([sQuery(id+"F0.wireOp",EDGE,"E0"),sQuery(id+"F0.wireOp",EDGE,"E8"),sQuery(id+"F0.wireOp",EDGE,"E9"),sQuery(id+"F0.wireOp",EDGE,"E12"),sQuery(id+"F0.wireOp",EDGE,"E14")])]}),"instanceName":"45"});
            var Q82;
            Q82=makeQuery(id+"F2.opPattern","COPY",BODY,{"derivedFrom":makeQuery(id+"F1.opExtrude","SWEPT_BODY",BODY,{"disambiguationData":[OSD([sQuery(id+"F0.wireOp",EDGE,"E0"),sQuery(id+"F0.wireOp",EDGE,"E8"),sQuery(id+"F0.wireOp",EDGE,"E9"),sQuery(id+"F0.wireOp",EDGE,"E12"),sQuery(id+"F0.wireOp",EDGE,"E14")])]}),"instanceName":"68"});
            var Q83;
            Q83=makeQuery(id+"F2.opPattern","COPY",BODY,{"derivedFrom":makeQuery(id+"F1.opExtrude","SWEPT_BODY",BODY,{"disambiguationData":[OSD([sQuery(id+"F0.wireOp",EDGE,"E0"),sQuery(id+"F0.wireOp",EDGE,"E8"),sQuery(id+"F0.wireOp",EDGE,"E9"),sQuery(id+"F0.wireOp",EDGE,"E12"),sQuery(id+"F0.wireOp",EDGE,"E14")])]}),"instanceName":"93"});
            var Q84;
            Q84=makeQuery(id+"F2.opPattern","COPY",BODY,{"derivedFrom":makeQuery(id+"F1.opExtrude","SWEPT_BODY",BODY,{"disambiguationData":[OSD([sQuery(id+"F0.wireOp",EDGE,"E0"),sQuery(id+"F0.wireOp",EDGE,"E8"),sQuery(id+"F0.wireOp",EDGE,"E9"),sQuery(id+"F0.wireOp",EDGE,"E12"),sQuery(id+"F0.wireOp",EDGE,"E14")])]}),"instanceName":"20"});
            var Q85;
            Q85=makeQuery(id+"F2.opPattern","COPY",BODY,{"derivedFrom":makeQuery(id+"F1.opExtrude","SWEPT_BODY",BODY,{"disambiguationData":[OSD([sQuery(id+"F0.wireOp",EDGE,"E0"),sQuery(id+"F0.wireOp",EDGE,"E8"),sQuery(id+"F0.wireOp",EDGE,"E9"),sQuery(id+"F0.wireOp",EDGE,"E12"),sQuery(id+"F0.wireOp",EDGE,"E14")])]}),"instanceName":"36"});
            var Q86;
            Q86=makeQuery(id+"F2.opPattern","COPY",BODY,{"derivedFrom":makeQuery(id+"F1.opExtrude","SWEPT_BODY",BODY,{"disambiguationData":[OSD([sQuery(id+"F0.wireOp",EDGE,"E0"),sQuery(id+"F0.wireOp",EDGE,"E8"),sQuery(id+"F0.wireOp",EDGE,"E9"),sQuery(id+"F0.wireOp",EDGE,"E12"),sQuery(id+"F0.wireOp",EDGE,"E14")])]}),"instanceName":"52"});
            var Q87;
            Q87=makeQuery(id+"F2.opPattern","COPY",BODY,{"derivedFrom":makeQuery(id+"F1.opExtrude","SWEPT_BODY",BODY,{"disambiguationData":[OSD([sQuery(id+"F0.wireOp",EDGE,"E0"),sQuery(id+"F0.wireOp",EDGE,"E8"),sQuery(id+"F0.wireOp",EDGE,"E9"),sQuery(id+"F0.wireOp",EDGE,"E12"),sQuery(id+"F0.wireOp",EDGE,"E14")])]}),"instanceName":"4"});
            var Q88;
            Q88=makeQuery(id+"F2.opPattern","COPY",BODY,{"derivedFrom":makeQuery(id+"F1.opExtrude","SWEPT_BODY",BODY,{"disambiguationData":[OSD([sQuery(id+"F0.wireOp",EDGE,"E0"),sQuery(id+"F0.wireOp",EDGE,"E8"),sQuery(id+"F0.wireOp",EDGE,"E9"),sQuery(id+"F0.wireOp",EDGE,"E12"),sQuery(id+"F0.wireOp",EDGE,"E14")])]}),"instanceName":"75"});
            var Q89;
            Q89=makeQuery(id+"F2.opPattern","COPY",BODY,{"derivedFrom":makeQuery(id+"F1.opExtrude","SWEPT_BODY",BODY,{"disambiguationData":[OSD([sQuery(id+"F0.wireOp",EDGE,"E0"),sQuery(id+"F0.wireOp",EDGE,"E8"),sQuery(id+"F0.wireOp",EDGE,"E9"),sQuery(id+"F0.wireOp",EDGE,"E12"),sQuery(id+"F0.wireOp",EDGE,"E14")])]}),"instanceName":"2"});
            var Q90;
            Q90=makeQuery(id+"F2.opPattern","COPY",BODY,{"derivedFrom":makeQuery(id+"F1.opExtrude","SWEPT_BODY",BODY,{"disambiguationData":[OSD([sQuery(id+"F0.wireOp",EDGE,"E0"),sQuery(id+"F0.wireOp",EDGE,"E8"),sQuery(id+"F0.wireOp",EDGE,"E9"),sQuery(id+"F0.wireOp",EDGE,"E12"),sQuery(id+"F0.wireOp",EDGE,"E14")])]}),"instanceName":"91"});
            var Q91;
            Q91=makeQuery(id+"F2.opPattern","COPY",BODY,{"derivedFrom":makeQuery(id+"F1.opExtrude","SWEPT_BODY",BODY,{"disambiguationData":[OSD([sQuery(id+"F0.wireOp",EDGE,"E0"),sQuery(id+"F0.wireOp",EDGE,"E8"),sQuery(id+"F0.wireOp",EDGE,"E9"),sQuery(id+"F0.wireOp",EDGE,"E12"),sQuery(id+"F0.wireOp",EDGE,"E14")])]}),"instanceName":"9"});
            var Q92;
            Q92=makeQuery(id+"F2.opPattern","COPY",BODY,{"derivedFrom":makeQuery(id+"F1.opExtrude","SWEPT_BODY",BODY,{"disambiguationData":[OSD([sQuery(id+"F0.wireOp",EDGE,"E0"),sQuery(id+"F0.wireOp",EDGE,"E8"),sQuery(id+"F0.wireOp",EDGE,"E9"),sQuery(id+"F0.wireOp",EDGE,"E12"),sQuery(id+"F0.wireOp",EDGE,"E14")])]}),"instanceName":"48"});
            var Q93;
            Q93=makeQuery(id+"F2.opPattern","COPY",BODY,{"derivedFrom":makeQuery(id+"F1.opExtrude","SWEPT_BODY",BODY,{"disambiguationData":[OSD([sQuery(id+"F0.wireOp",EDGE,"E0"),sQuery(id+"F0.wireOp",EDGE,"E8"),sQuery(id+"F0.wireOp",EDGE,"E9"),sQuery(id+"F0.wireOp",EDGE,"E12"),sQuery(id+"F0.wireOp",EDGE,"E14")])]}),"instanceName":"55"});
            var Q94;
            Q94=makeQuery(id+"F1.opExtrude","SWEPT_BODY",BODY,{"disambiguationData":[OSD([sQuery(id+"F0.wireOp",EDGE,"E0"),sQuery(id+"F0.wireOp",EDGE,"E8"),sQuery(id+"F0.wireOp",EDGE,"E9"),sQuery(id+"F0.wireOp",EDGE,"E12"),sQuery(id+"F0.wireOp",EDGE,"E14")])]});
            var Q95;
            Q95=makeQuery(id+"F2.opPattern","COPY",BODY,{"derivedFrom":makeQuery(id+"F1.opExtrude","SWEPT_BODY",BODY,{"disambiguationData":[OSD([sQuery(id+"F0.wireOp",EDGE,"E0"),sQuery(id+"F0.wireOp",EDGE,"E8"),sQuery(id+"F0.wireOp",EDGE,"E9"),sQuery(id+"F0.wireOp",EDGE,"E12"),sQuery(id+"F0.wireOp",EDGE,"E14")])]}),"instanceName":"1"});
            var Q96;
            Q96=makeQuery(id+"F3.opExtrude","SWEPT_BODY",BODY,{"disambiguationData":[OSD([sQuery(id+"F0.wireOp",EDGE,"E0")])]});
            booleanBodies(context, id + "F4", {"operationType" : BooleanOperationType.UNION, "tools" : qUnion([Q0, Q1, Q2, Q3, Q4, Q5, Q6, Q7, Q8, Q9, Q10, Q11, Q12, Q13, Q14, Q15, Q16, Q17, Q18, Q19, Q20, Q21, Q22, Q23, Q24, Q25, Q26, Q27, Q28, Q29, Q30, Q31, Q32, Q33, Q34, Q35, Q36, Q37, Q38, Q39, Q40, Q41, Q42, Q43, Q44, Q45, Q46, Q47, Q48, Q49, Q50, Q51, Q52, Q53, Q54, Q55, Q56, Q57, Q58, Q59, Q60, Q61, Q62, Q63, Q64, Q65, Q66, Q67, Q68, Q69, Q70, Q71, Q72, Q73, Q74, Q75, Q76, Q77, Q78, Q79, Q80, Q81, Q82, Q83, Q84, Q85, Q86, Q87, Q88, Q89, Q90, Q91, Q92, Q93, Q94, Q95, Q96])});
        }
        {
            var Q0;
            {var subQ0=sQuery(id+"F0.wireOp",EDGE,"E0");var subQ1=makeQuery(id+"F1.opExtrude","CAP_FACE",FACE,{"disambiguationData":[OSD([subQ0,sQuery(id+"F0.wireOp",EDGE,"E8"),sQuery(id+"F0.wireOp",EDGE,"E9"),sQuery(id+"F0.wireOp",EDGE,"E12"),sQuery(id+"F0.wireOp",EDGE,"E14")])],"isStart":false});Q0=makeQuery(id+"F4.opBoolean","MERGE",FACE,{"derivedFrom":[subQ1,makeQuery(id+"F2.opPattern","COPY",FACE,{"derivedFrom":subQ1,"instanceName":"1"}),makeQuery(id+"F2.opPattern","COPY",FACE,{"derivedFrom":subQ1,"instanceName":"2"}),makeQuery(id+"F2.opPattern","COPY",FACE,{"derivedFrom":subQ1,"instanceName":"3"}),makeQuery(id+"F2.opPattern","COPY",FACE,{"derivedFrom":subQ1,"instanceName":"4"}),makeQuery(id+"F2.opPattern","COPY",FACE,{"derivedFrom":subQ1,"instanceName":"5"}),makeQuery(id+"F2.opPattern","COPY",FACE,{"derivedFrom":subQ1,"instanceName":"6"}),makeQuery(id+"F2.opPattern","COPY",FACE,{"derivedFrom":subQ1,"instanceName":"7"}),makeQuery(id+"F2.opPattern","COPY",FACE,{"derivedFrom":subQ1,"instanceName":"8"}),makeQuery(id+"F2.opPattern","COPY",FACE,{"derivedFrom":subQ1,"instanceName":"9"}),makeQuery(id+"F2.opPattern","COPY",FACE,{"derivedFrom":subQ1,"instanceName":"10"}),makeQuery(id+"F2.opPattern","COPY",FACE,{"derivedFrom":subQ1,"instanceName":"11"}),makeQuery(id+"F2.opPattern","COPY",FACE,{"derivedFrom":subQ1,"instanceName":"12"}),makeQuery(id+"F2.opPattern","COPY",FACE,{"derivedFrom":subQ1,"instanceName":"13"}),makeQuery(id+"F2.opPattern","COPY",FACE,{"derivedFrom":subQ1,"instanceName":"14"}),makeQuery(id+"F2.opPattern","COPY",FACE,{"derivedFrom":subQ1,"instanceName":"15"}),makeQuery(id+"F2.opPattern","COPY",FACE,{"derivedFrom":subQ1,"instanceName":"16"}),makeQuery(id+"F2.opPattern","COPY",FACE,{"derivedFrom":subQ1,"instanceName":"17"}),makeQuery(id+"F2.opPattern","COPY",FACE,{"derivedFrom":subQ1,"instanceName":"18"}),makeQuery(id+"F2.opPattern","COPY",FACE,{"derivedFrom":subQ1,"instanceName":"19"}),makeQuery(id+"F2.opPattern","COPY",FACE,{"derivedFrom":subQ1,"instanceName":"20"}),makeQuery(id+"F2.opPattern","COPY",FACE,{"derivedFrom":subQ1,"instanceName":"21"}),makeQuery(id+"F2.opPattern","COPY",FACE,{"derivedFrom":subQ1,"instanceName":"22"}),makeQuery(id+"F2.opPattern","COPY",FACE,{"derivedFrom":subQ1,"instanceName":"23"}),makeQuery(id+"F2.opPattern","COPY",FACE,{"derivedFrom":subQ1,"instanceName":"24"}),makeQuery(id+"F2.opPattern","COPY",FACE,{"derivedFrom":subQ1,"instanceName":"25"}),makeQuery(id+"F2.opPattern","COPY",FACE,{"derivedFrom":subQ1,"instanceName":"26"}),makeQuery(id+"F2.opPattern","COPY",FACE,{"derivedFrom":subQ1,"instanceName":"27"}),makeQuery(id+"F2.opPattern","COPY",FACE,{"derivedFrom":subQ1,"instanceName":"28"}),makeQuery(id+"F2.opPattern","COPY",FACE,{"derivedFrom":subQ1,"instanceName":"29"}),makeQuery(id+"F2.opPattern","COPY",FACE,{"derivedFrom":subQ1,"instanceName":"30"}),makeQuery(id+"F2.opPattern","COPY",FACE,{"derivedFrom":subQ1,"instanceName":"31"}),makeQuery(id+"F2.opPattern","COPY",FACE,{"derivedFrom":subQ1,"instanceName":"32"}),makeQuery(id+"F2.opPattern","COPY",FACE,{"derivedFrom":subQ1,"instanceName":"33"}),makeQuery(id+"F2.opPattern","COPY",FACE,{"derivedFrom":subQ1,"instanceName":"34"}),makeQuery(id+"F2.opPattern","COPY",FACE,{"derivedFrom":subQ1,"instanceName":"35"}),makeQuery(id+"F2.opPattern","COPY",FACE,{"derivedFrom":subQ1,"instanceName":"36"}),makeQuery(id+"F2.opPattern","COPY",FACE,{"derivedFrom":subQ1,"instanceName":"37"}),makeQuery(id+"F2.opPattern","COPY",FACE,{"derivedFrom":subQ1,"instanceName":"38"}),makeQuery(id+"F2.opPattern","COPY",FACE,{"derivedFrom":subQ1,"instanceName":"39"}),makeQuery(id+"F2.opPattern","COPY",FACE,{"derivedFrom":subQ1,"instanceName":"40"}),makeQuery(id+"F2.opPattern","COPY",FACE,{"derivedFrom":subQ1,"instanceName":"41"}),makeQuery(id+"F2.opPattern","COPY",FACE,{"derivedFrom":subQ1,"instanceName":"42"}),makeQuery(id+"F2.opPattern","COPY",FACE,{"derivedFrom":subQ1,"instanceName":"43"}),makeQuery(id+"F2.opPattern","COPY",FACE,{"derivedFrom":subQ1,"instanceName":"44"}),makeQuery(id+"F2.opPattern","COPY",FACE,{"derivedFrom":subQ1,"instanceName":"45"}),makeQuery(id+"F2.opPattern","COPY",FACE,{"derivedFrom":subQ1,"instanceName":"46"}),makeQuery(id+"F2.opPattern","COPY",FACE,{"derivedFrom":subQ1,"instanceName":"47"}),makeQuery(id+"F2.opPattern","COPY",FACE,{"derivedFrom":subQ1,"instanceName":"48"}),makeQuery(id+"F2.opPattern","COPY",FACE,{"derivedFrom":subQ1,"instanceName":"49"}),makeQuery(id+"F2.opPattern","COPY",FACE,{"derivedFrom":subQ1,"instanceName":"50"}),makeQuery(id+"F2.opPattern","COPY",FACE,{"derivedFrom":subQ1,"instanceName":"51"}),makeQuery(id+"F2.opPattern","COPY",FACE,{"derivedFrom":subQ1,"instanceName":"52"}),makeQuery(id+"F2.opPattern","COPY",FACE,{"derivedFrom":subQ1,"instanceName":"53"}),makeQuery(id+"F2.opPattern","COPY",FACE,{"derivedFrom":subQ1,"instanceName":"54"}),makeQuery(id+"F2.opPattern","COPY",FACE,{"derivedFrom":subQ1,"instanceName":"55"}),makeQuery(id+"F2.opPattern","COPY",FACE,{"derivedFrom":subQ1,"instanceName":"56"}),makeQuery(id+"F2.opPattern","COPY",FACE,{"derivedFrom":subQ1,"instanceName":"57"}),makeQuery(id+"F2.opPattern","COPY",FACE,{"derivedFrom":subQ1,"instanceName":"58"}),makeQuery(id+"F2.opPattern","COPY",FACE,{"derivedFrom":subQ1,"instanceName":"59"}),makeQuery(id+"F2.opPattern","COPY",FACE,{"derivedFrom":subQ1,"instanceName":"60"}),makeQuery(id+"F2.opPattern","COPY",FACE,{"derivedFrom":subQ1,"instanceName":"61"}),makeQuery(id+"F2.opPattern","COPY",FACE,{"derivedFrom":subQ1,"instanceName":"62"}),makeQuery(id+"F2.opPattern","COPY",FACE,{"derivedFrom":subQ1,"instanceName":"63"}),makeQuery(id+"F2.opPattern","COPY",FACE,{"derivedFrom":subQ1,"instanceName":"64"}),makeQuery(id+"F2.opPattern","COPY",FACE,{"derivedFrom":subQ1,"instanceName":"65"}),makeQuery(id+"F2.opPattern","COPY",FACE,{"derivedFrom":subQ1,"instanceName":"66"}),makeQuery(id+"F2.opPattern","COPY",FACE,{"derivedFrom":subQ1,"instanceName":"67"}),makeQuery(id+"F2.opPattern","COPY",FACE,{"derivedFrom":subQ1,"instanceName":"68"}),makeQuery(id+"F2.opPattern","COPY",FACE,{"derivedFrom":subQ1,"instanceName":"69"}),makeQuery(id+"F2.opPattern","COPY",FACE,{"derivedFrom":subQ1,"instanceName":"70"}),makeQuery(id+"F2.opPattern","COPY",FACE,{"derivedFrom":subQ1,"instanceName":"71"}),makeQuery(id+"F2.opPattern","COPY",FACE,{"derivedFrom":subQ1,"instanceName":"72"}),makeQuery(id+"F2.opPattern","COPY",FACE,{"derivedFrom":subQ1,"instanceName":"73"}),makeQuery(id+"F2.opPattern","COPY",FACE,{"derivedFrom":subQ1,"instanceName":"74"}),makeQuery(id+"F2.opPattern","COPY",FACE,{"derivedFrom":subQ1,"instanceName":"75"}),makeQuery(id+"F2.opPattern","COPY",FACE,{"derivedFrom":subQ1,"instanceName":"76"}),makeQuery(id+"F2.opPattern","COPY",FACE,{"derivedFrom":subQ1,"instanceName":"77"}),makeQuery(id+"F2.opPattern","COPY",FACE,{"derivedFrom":subQ1,"instanceName":"78"}),makeQuery(id+"F2.opPattern","COPY",FACE,{"derivedFrom":subQ1,"instanceName":"79"}),makeQuery(id+"F2.opPattern","COPY",FACE,{"derivedFrom":subQ1,"instanceName":"80"}),makeQuery(id+"F2.opPattern","COPY",FACE,{"derivedFrom":subQ1,"instanceName":"81"}),makeQuery(id+"F2.opPattern","COPY",FACE,{"derivedFrom":subQ1,"instanceName":"82"}),makeQuery(id+"F2.opPattern","COPY",FACE,{"derivedFrom":subQ1,"instanceName":"83"}),makeQuery(id+"F2.opPattern","COPY",FACE,{"derivedFrom":subQ1,"instanceName":"84"}),makeQuery(id+"F2.opPattern","COPY",FACE,{"derivedFrom":subQ1,"instanceName":"85"}),makeQuery(id+"F2.opPattern","COPY",FACE,{"derivedFrom":subQ1,"instanceName":"86"}),makeQuery(id+"F2.opPattern","COPY",FACE,{"derivedFrom":subQ1,"instanceName":"87"}),makeQuery(id+"F2.opPattern","COPY",FACE,{"derivedFrom":subQ1,"instanceName":"88"}),makeQuery(id+"F2.opPattern","COPY",FACE,{"derivedFrom":subQ1,"instanceName":"89"}),makeQuery(id+"F2.opPattern","COPY",FACE,{"derivedFrom":subQ1,"instanceName":"90"}),makeQuery(id+"F2.opPattern","COPY",FACE,{"derivedFrom":subQ1,"instanceName":"91"}),makeQuery(id+"F2.opPattern","COPY",FACE,{"derivedFrom":subQ1,"instanceName":"92"}),makeQuery(id+"F2.opPattern","COPY",FACE,{"derivedFrom":subQ1,"instanceName":"93"}),makeQuery(id+"F2.opPattern","COPY",FACE,{"derivedFrom":subQ1,"instanceName":"94"}),makeQuery(id+"F2.opPattern","COPY",FACE,{"derivedFrom":subQ1,"instanceName":"95"}),makeQuery(id+"F3.opExtrude","CAP_FACE",FACE,{"disambiguationData":[OSD([subQ0])],"isStart":false})]});}
            var sketch = newSketch(context, id + "F5", { "sketchPlane" : qUnion([Q0])});
            skCircle(sketch, "E15", {"center": v(0, 0) * mm, "radius": 0.68 * mm});
            skCircle(sketch, "E16", {"center": v(0, 0) * mm, "radius": 3.6 * mm, "construction": true});
            skCircle(sketch, "E17", {"center": v(0, 0) * mm, "radius": 0.8 * mm, "construction": true});
            skLineSegment(sketch, "E18", {"start": v(0, 0) * mm, "end": v(0, 3.6) * mm, "construction": true});
            skLineSegment(sketch, "E19.0", {"start": v(0, 3.6) * mm, "end": v(3.42, 1.11) * mm, "construction": true});
            skLineSegment(sketch, "E19.1", {"start": v(3.42, 1.11) * mm, "end": v(2.12, -2.91) * mm, "construction": true});
            skLineSegment(sketch, "E19.2", {"start": v(2.12, -2.91) * mm, "end": v(-2.12, -2.91) * mm, "construction": true});
            skLineSegment(sketch, "E19.3", {"start": v(-2.12, -2.91) * mm, "end": v(-3.42, 1.11) * mm, "construction": true});
            skLineSegment(sketch, "E19.4", {"start": v(-3.42, 1.11) * mm, "end": v(0, 3.6) * mm, "construction": true});
            skLineSegment(sketch, "E20", {"start": v(0, 0) * mm, "end": v(0, -3.6) * mm, "construction": true});
            skLineSegment(sketch, "E21.0", {"start": v(0.58, -0.8) * mm, "end": v(-0.58, -0.8) * mm, "construction": true});
            skLineSegment(sketch, "E21.1", {"start": v(-0.58, -0.8) * mm, "end": v(-0.94, 0.3) * mm, "construction": true});
            skLineSegment(sketch, "E21.2", {"start": v(-0.94, 0.3) * mm, "end": v(0, 0.99) * mm, "construction": true});
            skLineSegment(sketch, "E21.3", {"start": v(0, 0.99) * mm, "end": v(0.94, 0.3) * mm, "construction": true});
            skLineSegment(sketch, "E21.4", {"start": v(0.94, 0.3) * mm, "end": v(0.58, -0.8) * mm, "construction": true});
            skPoint(sketch, "E21.0.midPoint", {"position": v(0, -0.8) * mm});
            skCircle(sketch, "E22", {"center": v(0, 0.99) * mm, "radius": 0.25 * mm, "construction": true});
            skCircle(sketch, "E23", {"center": v(0, 3.6) * mm, "radius": 0.12 * mm, "construction": true});
            skCircle(sketch, "E24", {"center": v(0.94, 0.3) * mm, "radius": 0.25 * mm, "construction": true});
            skCircle(sketch, "E25", {"center": v(0.58, -0.8) * mm, "radius": 0.25 * mm, "construction": true});
            skCircle(sketch, "E26", {"center": v(-0.58, -0.8) * mm, "radius": 0.25 * mm, "construction": true});
            skCircle(sketch, "E27", {"center": v(-0.94, 0.3) * mm, "radius": 0.25 * mm, "construction": true});
            skCircle(sketch, "E28", {"center": v(-3.42, 1.11) * mm, "radius": 0.12 * mm, "construction": true});
            skCircle(sketch, "E29", {"center": v(-2.12, -2.91) * mm, "radius": 0.12 * mm, "construction": true});
            skCircle(sketch, "E30", {"center": v(2.12, -2.91) * mm, "radius": 0.12 * mm, "construction": true});
            skCircle(sketch, "E31", {"center": v(3.42, 1.11) * mm, "radius": 0.12 * mm, "construction": true});
            skLineSegment(sketch, "E32", {"start": v(-0.12, 3.6) * mm, "end": v(-0.25, 1) * mm});
            skLineSegment(sketch, "E33", {"start": v(0.12, 3.6) * mm, "end": v(0.25, 1) * mm});
            skLineSegment(sketch, "E34", {"start": v(3.4, 1.23) * mm, "end": v(0.87, 0.55) * mm});
            skLineSegment(sketch, "E35", {"start": v(3.47, 1) * mm, "end": v(1.03, 0.07) * mm});
            skArc(sketch, "E36", {"start": v(0.25, 1) * mm, "mid": v(0.6, 0.83) * mm, "end": v(0.87, 0.55) * mm});
            skArc(sketch, "E37", {"start": v(0.12, 3.6) * mm, "mid": v(2.12, 2.92) * mm, "end": v(3.4, 1.23) * mm});
            skLineSegment(sketch, "E38", {"start": v(2.22, -2.84) * mm, "end": v(0.8, -0.66) * mm});
            skLineSegment(sketch, "E39", {"start": v(2.02, -3) * mm, "end": v(0.39, -0.96) * mm});
            skLineSegment(sketch, "E40", {"start": v(-2.02, -3) * mm, "end": v(-0.39, -0.96) * mm});
            skLineSegment(sketch, "E41", {"start": v(-2.22, -2.84) * mm, "end": v(-0.8, -0.66) * mm});
            skLineSegment(sketch, "E42", {"start": v(-3.47, 1) * mm, "end": v(-1.03, 0.07) * mm});
            skLineSegment(sketch, "E43", {"start": v(-3.4, 1.23) * mm, "end": v(-0.87, 0.55) * mm});
            skArc(sketch, "E44", {"start": v(1.03, 0.07) * mm, "mid": v(0.98, -0.32) * mm, "end": v(0.8, -0.66) * mm});
            skArc(sketch, "E45", {"start": v(0.39, -0.96) * mm, "mid": v(0, -1.03) * mm, "end": v(-0.39, -0.96) * mm});
            skArc(sketch, "E46", {"start": v(-0.8, -0.66) * mm, "mid": v(-0.98, -0.32) * mm, "end": v(-1.03, 0.07) * mm});
            skArc(sketch, "E47", {"start": v(-0.87, 0.55) * mm, "mid": v(-0.6, 0.83) * mm, "end": v(-0.25, 1) * mm});
            skArc(sketch, "E48", {"start": v(3.47, 1) * mm, "mid": v(3.43, -1.11) * mm, "end": v(2.22, -2.84) * mm});
            skArc(sketch, "E49", {"start": v(2.02, -3) * mm, "mid": v(0, -3.6) * mm, "end": v(-2.02, -3) * mm});
            skArc(sketch, "E50", {"start": v(-2.22, -2.84) * mm, "mid": v(-3.43, -1.11) * mm, "end": v(-3.47, 1) * mm});
            skArc(sketch, "E51", {"start": v(-3.4, 1.23) * mm, "mid": v(-2.12, 2.92) * mm, "end": v(-0.12, 3.6) * mm});
            skSolve(sketch);
        }
        {
            var Q0;
            Q0=qSketchRegion(id+"F5",true);
            extrude(context, id + "F6", {"entities" : qUnion([Q0]), "operationType" : NewBodyOperationType.REMOVE, "endBound" : BoundingType.THROUGH_ALL, "oppositeDirection" : true, "depth" : 25 * mm});
        }
        {
            var Q0;
            Q0=qCreatedBy(makeId("Top.planeOp"),FACE);
            var sketch = newSketch(context, id + "F7", { "sketchPlane" : qUnion([Q0])});
            skCircle(sketch, "E52", {"center": v(0, 0) * mm, "radius": 0.59 * mm, "construction": true});
            skCircle(sketch, "E53", {"center": v(0, 0) * mm, "radius": 0.9 * mm, "construction": true});
            skCircle(sketch, "E54", {"center": v(0, 0) * mm, "radius": 1.02 * mm, "construction": true});
            skLineSegment(sketch, "E55", {"start": v(0, 0.9) * mm, "end": v(0.1, 0.9) * mm, "construction": true});
            skLineSegment(sketch, "E56", {"start": v(0, 0.9) * mm, "end": v(-0.1, 0.9) * mm, "construction": true});
            skLineSegment(sketch, "E57", {"start": v(-0.1, 0.9) * mm, "end": v(0, 0) * mm, "construction": true});
            skLineSegment(sketch, "E58", {"start": v(0.1, 0.9) * mm, "end": v(0, 0) * mm, "construction": true});
            skLineSegment(sketch, "E59", {"start": v(-0.1, 0.9) * mm, "end": v(-0.06, 0.58) * mm});
            skLineSegment(sketch, "E60", {"start": v(0.1, 0.9) * mm, "end": v(0.06, 0.58) * mm});
            skCircle(sketch, "E61", {"center": v(-0.1, 0.9) * mm, "radius": 0.12 * mm, "construction": true});
            skCircle(sketch, "E62", {"center": v(0.1, 0.9) * mm, "radius": 0.12 * mm, "construction": true});
            skCircle(sketch, "E63", {"center": v(0, 1.02) * mm, "radius": 0.12 * mm, "construction": true});
            skArc(sketch, "E64", {"start": v(0.1, 0.9) * mm, "mid": v(0.07, 0.98) * mm, "end": v(0, 1.02) * mm});
            skArc(sketch, "E65", {"start": v(-0.1, 0.9) * mm, "mid": v(-0.07, 0.98) * mm, "end": v(0, 1.02) * mm});
            skCircle(sketch, "E66", {"center": v(0, 0) * mm, "radius": 0.59 * mm});
            skSolve(sketch);
        }
        {
            var Q0;
            {var subQ0=sQuery(id+"F7.wireOp",EDGE,"E59");Q0=makeQuery(id+"F7.imprint","IMPRINT",FACE,{"disambiguationData":[TD([[makeQuery(id+"F7.imprint","IMPRINT",EDGE,{"derivedFrom":subQ0}),1.0]])]});}
            extrude(context, id + "F8", {"entities" : qUnion([Q0]), "depth" : 1 * mm});
        }
        {
            var Q0;
            Q0=makeQuery(id+"F8.opExtrude","SWEPT_BODY",BODY,{"disambiguationData":[OSD([sQuery(id+"F7.wireOp",EDGE,"E59"),sQuery(id+"F7.wireOp",EDGE,"E60"),sQuery(id+"F7.wireOp",EDGE,"E64"),sQuery(id+"F7.wireOp",EDGE,"E65"),sQuery(id+"F7.wireOp",EDGE,"E66")])]});
            var Q1;
            Q1=makeQuery(id+"F8.opExtrude","CAP_EDGE",EDGE,{"disambiguationData":[OSD([sQuery(id+"F7.wireOp",EDGE,"E66")])],"isStart":false});
            circularPattern(context, id + "F9", {"entities" : qUnion([Q0]), "axis" : qUnion([Q1]), "angle" : 30 * degree, "instanceCount" : round(12)});
        }
        {
            var Q0;
            {var subQ0=sQuery(id+"F7.wireOp",EDGE,"E66");var subQ2=makeQuery(id+"F7.imprint","INTERSECT",VERTEX,{"derivedFrom":[sQuery(id+"F7.wireOp",EDGE,"E59"),subQ0]});Q0=makeQuery(id+"F7.imprint","IMPRINT",FACE,{"disambiguationData":[TD([[makeQuery(id+"F7.imprint","IMPRINT",EDGE,{"disambiguationData":[TD([[subQ2,1.0]])],"derivedFrom":subQ0}),1.0]])]});}
            extrude(context, id + "F10", {"entities" : qUnion([Q0]), "depth" : 2 * mm});
        }
        {
            var Q0;
            Q0=makeQuery(id+"F8.opExtrude","SWEPT_BODY",BODY,{"disambiguationData":[OSD([sQuery(id+"F7.wireOp",EDGE,"E59"),sQuery(id+"F7.wireOp",EDGE,"E60"),sQuery(id+"F7.wireOp",EDGE,"E64"),sQuery(id+"F7.wireOp",EDGE,"E65"),sQuery(id+"F7.wireOp",EDGE,"E66")])]});
            var Q1;
            Q1=makeQuery(id+"F9.opPattern","COPY",BODY,{"derivedFrom":makeQuery(id+"F8.opExtrude","SWEPT_BODY",BODY,{"disambiguationData":[OSD([sQuery(id+"F7.wireOp",EDGE,"E59"),sQuery(id+"F7.wireOp",EDGE,"E60"),sQuery(id+"F7.wireOp",EDGE,"E64"),sQuery(id+"F7.wireOp",EDGE,"E65"),sQuery(id+"F7.wireOp",EDGE,"E66")])]}),"instanceName":"6"});
            var Q2;
            Q2=makeQuery(id+"F9.opPattern","COPY",BODY,{"derivedFrom":makeQuery(id+"F8.opExtrude","SWEPT_BODY",BODY,{"disambiguationData":[OSD([sQuery(id+"F7.wireOp",EDGE,"E59"),sQuery(id+"F7.wireOp",EDGE,"E60"),sQuery(id+"F7.wireOp",EDGE,"E64"),sQuery(id+"F7.wireOp",EDGE,"E65"),sQuery(id+"F7.wireOp",EDGE,"E66")])]}),"instanceName":"11"});
            var Q3;
            Q3=makeQuery(id+"F9.opPattern","COPY",BODY,{"derivedFrom":makeQuery(id+"F8.opExtrude","SWEPT_BODY",BODY,{"disambiguationData":[OSD([sQuery(id+"F7.wireOp",EDGE,"E59"),sQuery(id+"F7.wireOp",EDGE,"E60"),sQuery(id+"F7.wireOp",EDGE,"E64"),sQuery(id+"F7.wireOp",EDGE,"E65"),sQuery(id+"F7.wireOp",EDGE,"E66")])]}),"instanceName":"9"});
            var Q4;
            Q4=makeQuery(id+"F9.opPattern","COPY",BODY,{"derivedFrom":makeQuery(id+"F8.opExtrude","SWEPT_BODY",BODY,{"disambiguationData":[OSD([sQuery(id+"F7.wireOp",EDGE,"E59"),sQuery(id+"F7.wireOp",EDGE,"E60"),sQuery(id+"F7.wireOp",EDGE,"E64"),sQuery(id+"F7.wireOp",EDGE,"E65"),sQuery(id+"F7.wireOp",EDGE,"E66")])]}),"instanceName":"10"});
            var Q5;
            Q5=makeQuery(id+"F9.opPattern","COPY",BODY,{"derivedFrom":makeQuery(id+"F8.opExtrude","SWEPT_BODY",BODY,{"disambiguationData":[OSD([sQuery(id+"F7.wireOp",EDGE,"E59"),sQuery(id+"F7.wireOp",EDGE,"E60"),sQuery(id+"F7.wireOp",EDGE,"E64"),sQuery(id+"F7.wireOp",EDGE,"E65"),sQuery(id+"F7.wireOp",EDGE,"E66")])]}),"instanceName":"8"});
            var Q6;
            Q6=makeQuery(id+"F9.opPattern","COPY",BODY,{"derivedFrom":makeQuery(id+"F8.opExtrude","SWEPT_BODY",BODY,{"disambiguationData":[OSD([sQuery(id+"F7.wireOp",EDGE,"E59"),sQuery(id+"F7.wireOp",EDGE,"E60"),sQuery(id+"F7.wireOp",EDGE,"E64"),sQuery(id+"F7.wireOp",EDGE,"E65"),sQuery(id+"F7.wireOp",EDGE,"E66")])]}),"instanceName":"5"});
            var Q7;
            Q7=makeQuery(id+"F9.opPattern","COPY",BODY,{"derivedFrom":makeQuery(id+"F8.opExtrude","SWEPT_BODY",BODY,{"disambiguationData":[OSD([sQuery(id+"F7.wireOp",EDGE,"E59"),sQuery(id+"F7.wireOp",EDGE,"E60"),sQuery(id+"F7.wireOp",EDGE,"E64"),sQuery(id+"F7.wireOp",EDGE,"E65"),sQuery(id+"F7.wireOp",EDGE,"E66")])]}),"instanceName":"3"});
            var Q8;
            Q8=makeQuery(id+"F9.opPattern","COPY",BODY,{"derivedFrom":makeQuery(id+"F8.opExtrude","SWEPT_BODY",BODY,{"disambiguationData":[OSD([sQuery(id+"F7.wireOp",EDGE,"E59"),sQuery(id+"F7.wireOp",EDGE,"E60"),sQuery(id+"F7.wireOp",EDGE,"E64"),sQuery(id+"F7.wireOp",EDGE,"E65"),sQuery(id+"F7.wireOp",EDGE,"E66")])]}),"instanceName":"7"});
            var Q9;
            Q9=makeQuery(id+"F9.opPattern","COPY",BODY,{"derivedFrom":makeQuery(id+"F8.opExtrude","SWEPT_BODY",BODY,{"disambiguationData":[OSD([sQuery(id+"F7.wireOp",EDGE,"E59"),sQuery(id+"F7.wireOp",EDGE,"E60"),sQuery(id+"F7.wireOp",EDGE,"E64"),sQuery(id+"F7.wireOp",EDGE,"E65"),sQuery(id+"F7.wireOp",EDGE,"E66")])]}),"instanceName":"1"});
            var Q10;
            Q10=makeQuery(id+"F9.opPattern","COPY",BODY,{"derivedFrom":makeQuery(id+"F8.opExtrude","SWEPT_BODY",BODY,{"disambiguationData":[OSD([sQuery(id+"F7.wireOp",EDGE,"E59"),sQuery(id+"F7.wireOp",EDGE,"E60"),sQuery(id+"F7.wireOp",EDGE,"E64"),sQuery(id+"F7.wireOp",EDGE,"E65"),sQuery(id+"F7.wireOp",EDGE,"E66")])]}),"instanceName":"2"});
            var Q11;
            Q11=makeQuery(id+"F9.opPattern","COPY",BODY,{"derivedFrom":makeQuery(id+"F8.opExtrude","SWEPT_BODY",BODY,{"disambiguationData":[OSD([sQuery(id+"F7.wireOp",EDGE,"E59"),sQuery(id+"F7.wireOp",EDGE,"E60"),sQuery(id+"F7.wireOp",EDGE,"E64"),sQuery(id+"F7.wireOp",EDGE,"E65"),sQuery(id+"F7.wireOp",EDGE,"E66")])]}),"instanceName":"4"});
            var Q12;
            Q12=makeQuery(id+"F10.opExtrude","SWEPT_BODY",BODY,{"disambiguationData":[OSD([sQuery(id+"F7.wireOp",EDGE,"E66")])]});
            booleanBodies(context, id + "F11", {"operationType" : BooleanOperationType.UNION, "tools" : qUnion([Q0, Q1, Q2, Q3, Q4, Q5, Q6, Q7, Q8, Q9, Q10, Q11, Q12])});
        }
        {
            var Q0;
            {var subQ0=sQuery(id+"F0.wireOp",EDGE,"E0");var subQ1=makeQuery(id+"F1.opExtrude","CAP_FACE",FACE,{"disambiguationData":[OSD([subQ0,sQuery(id+"F0.wireOp",EDGE,"E8"),sQuery(id+"F0.wireOp",EDGE,"E9"),sQuery(id+"F0.wireOp",EDGE,"E12"),sQuery(id+"F0.wireOp",EDGE,"E14")])],"isStart":false});Q0=makeQuery(id+"F4.opBoolean","MERGE",FACE,{"derivedFrom":[subQ1,makeQuery(id+"F2.opPattern","COPY",FACE,{"derivedFrom":subQ1,"instanceName":"1"}),makeQuery(id+"F2.opPattern","COPY",FACE,{"derivedFrom":subQ1,"instanceName":"2"}),makeQuery(id+"F2.opPattern","COPY",FACE,{"derivedFrom":subQ1,"instanceName":"3"}),makeQuery(id+"F2.opPattern","COPY",FACE,{"derivedFrom":subQ1,"instanceName":"4"}),makeQuery(id+"F2.opPattern","COPY",FACE,{"derivedFrom":subQ1,"instanceName":"5"}),makeQuery(id+"F2.opPattern","COPY",FACE,{"derivedFrom":subQ1,"instanceName":"6"}),makeQuery(id+"F2.opPattern","COPY",FACE,{"derivedFrom":subQ1,"instanceName":"7"}),makeQuery(id+"F2.opPattern","COPY",FACE,{"derivedFrom":subQ1,"instanceName":"8"}),makeQuery(id+"F2.opPattern","COPY",FACE,{"derivedFrom":subQ1,"instanceName":"9"}),makeQuery(id+"F2.opPattern","COPY",FACE,{"derivedFrom":subQ1,"instanceName":"10"}),makeQuery(id+"F2.opPattern","COPY",FACE,{"derivedFrom":subQ1,"instanceName":"11"}),makeQuery(id+"F2.opPattern","COPY",FACE,{"derivedFrom":subQ1,"instanceName":"12"}),makeQuery(id+"F2.opPattern","COPY",FACE,{"derivedFrom":subQ1,"instanceName":"13"}),makeQuery(id+"F2.opPattern","COPY",FACE,{"derivedFrom":subQ1,"instanceName":"14"}),makeQuery(id+"F2.opPattern","COPY",FACE,{"derivedFrom":subQ1,"instanceName":"15"}),makeQuery(id+"F2.opPattern","COPY",FACE,{"derivedFrom":subQ1,"instanceName":"16"}),makeQuery(id+"F2.opPattern","COPY",FACE,{"derivedFrom":subQ1,"instanceName":"17"}),makeQuery(id+"F2.opPattern","COPY",FACE,{"derivedFrom":subQ1,"instanceName":"18"}),makeQuery(id+"F2.opPattern","COPY",FACE,{"derivedFrom":subQ1,"instanceName":"19"}),makeQuery(id+"F2.opPattern","COPY",FACE,{"derivedFrom":subQ1,"instanceName":"20"}),makeQuery(id+"F2.opPattern","COPY",FACE,{"derivedFrom":subQ1,"instanceName":"21"}),makeQuery(id+"F2.opPattern","COPY",FACE,{"derivedFrom":subQ1,"instanceName":"22"}),makeQuery(id+"F2.opPattern","COPY",FACE,{"derivedFrom":subQ1,"instanceName":"23"}),makeQuery(id+"F2.opPattern","COPY",FACE,{"derivedFrom":subQ1,"instanceName":"24"}),makeQuery(id+"F2.opPattern","COPY",FACE,{"derivedFrom":subQ1,"instanceName":"25"}),makeQuery(id+"F2.opPattern","COPY",FACE,{"derivedFrom":subQ1,"instanceName":"26"}),makeQuery(id+"F2.opPattern","COPY",FACE,{"derivedFrom":subQ1,"instanceName":"27"}),makeQuery(id+"F2.opPattern","COPY",FACE,{"derivedFrom":subQ1,"instanceName":"28"}),makeQuery(id+"F2.opPattern","COPY",FACE,{"derivedFrom":subQ1,"instanceName":"29"}),makeQuery(id+"F2.opPattern","COPY",FACE,{"derivedFrom":subQ1,"instanceName":"30"}),makeQuery(id+"F2.opPattern","COPY",FACE,{"derivedFrom":subQ1,"instanceName":"31"}),makeQuery(id+"F2.opPattern","COPY",FACE,{"derivedFrom":subQ1,"instanceName":"32"}),makeQuery(id+"F2.opPattern","COPY",FACE,{"derivedFrom":subQ1,"instanceName":"33"}),makeQuery(id+"F2.opPattern","COPY",FACE,{"derivedFrom":subQ1,"instanceName":"34"}),makeQuery(id+"F2.opPattern","COPY",FACE,{"derivedFrom":subQ1,"instanceName":"35"}),makeQuery(id+"F2.opPattern","COPY",FACE,{"derivedFrom":subQ1,"instanceName":"36"}),makeQuery(id+"F2.opPattern","COPY",FACE,{"derivedFrom":subQ1,"instanceName":"37"}),makeQuery(id+"F2.opPattern","COPY",FACE,{"derivedFrom":subQ1,"instanceName":"38"}),makeQuery(id+"F2.opPattern","COPY",FACE,{"derivedFrom":subQ1,"instanceName":"39"}),makeQuery(id+"F2.opPattern","COPY",FACE,{"derivedFrom":subQ1,"instanceName":"40"}),makeQuery(id+"F2.opPattern","COPY",FACE,{"derivedFrom":subQ1,"instanceName":"41"}),makeQuery(id+"F2.opPattern","COPY",FACE,{"derivedFrom":subQ1,"instanceName":"42"}),makeQuery(id+"F2.opPattern","COPY",FACE,{"derivedFrom":subQ1,"instanceName":"43"}),makeQuery(id+"F2.opPattern","COPY",FACE,{"derivedFrom":subQ1,"instanceName":"44"}),makeQuery(id+"F2.opPattern","COPY",FACE,{"derivedFrom":subQ1,"instanceName":"45"}),makeQuery(id+"F2.opPattern","COPY",FACE,{"derivedFrom":subQ1,"instanceName":"46"}),makeQuery(id+"F2.opPattern","COPY",FACE,{"derivedFrom":subQ1,"instanceName":"47"}),makeQuery(id+"F2.opPattern","COPY",FACE,{"derivedFrom":subQ1,"instanceName":"48"}),makeQuery(id+"F2.opPattern","COPY",FACE,{"derivedFrom":subQ1,"instanceName":"49"}),makeQuery(id+"F2.opPattern","COPY",FACE,{"derivedFrom":subQ1,"instanceName":"50"}),makeQuery(id+"F2.opPattern","COPY",FACE,{"derivedFrom":subQ1,"instanceName":"51"}),makeQuery(id+"F2.opPattern","COPY",FACE,{"derivedFrom":subQ1,"instanceName":"52"}),makeQuery(id+"F2.opPattern","COPY",FACE,{"derivedFrom":subQ1,"instanceName":"53"}),makeQuery(id+"F2.opPattern","COPY",FACE,{"derivedFrom":subQ1,"instanceName":"54"}),makeQuery(id+"F2.opPattern","COPY",FACE,{"derivedFrom":subQ1,"instanceName":"55"}),makeQuery(id+"F2.opPattern","COPY",FACE,{"derivedFrom":subQ1,"instanceName":"56"}),makeQuery(id+"F2.opPattern","COPY",FACE,{"derivedFrom":subQ1,"instanceName":"57"}),makeQuery(id+"F2.opPattern","COPY",FACE,{"derivedFrom":subQ1,"instanceName":"58"}),makeQuery(id+"F2.opPattern","COPY",FACE,{"derivedFrom":subQ1,"instanceName":"59"}),makeQuery(id+"F2.opPattern","COPY",FACE,{"derivedFrom":subQ1,"instanceName":"60"}),makeQuery(id+"F2.opPattern","COPY",FACE,{"derivedFrom":subQ1,"instanceName":"61"}),makeQuery(id+"F2.opPattern","COPY",FACE,{"derivedFrom":subQ1,"instanceName":"62"}),makeQuery(id+"F2.opPattern","COPY",FACE,{"derivedFrom":subQ1,"instanceName":"63"}),makeQuery(id+"F2.opPattern","COPY",FACE,{"derivedFrom":subQ1,"instanceName":"64"}),makeQuery(id+"F2.opPattern","COPY",FACE,{"derivedFrom":subQ1,"instanceName":"65"}),makeQuery(id+"F2.opPattern","COPY",FACE,{"derivedFrom":subQ1,"instanceName":"66"}),makeQuery(id+"F2.opPattern","COPY",FACE,{"derivedFrom":subQ1,"instanceName":"67"}),makeQuery(id+"F2.opPattern","COPY",FACE,{"derivedFrom":subQ1,"instanceName":"68"}),makeQuery(id+"F2.opPattern","COPY",FACE,{"derivedFrom":subQ1,"instanceName":"69"}),makeQuery(id+"F2.opPattern","COPY",FACE,{"derivedFrom":subQ1,"instanceName":"70"}),makeQuery(id+"F2.opPattern","COPY",FACE,{"derivedFrom":subQ1,"instanceName":"71"}),makeQuery(id+"F2.opPattern","COPY",FACE,{"derivedFrom":subQ1,"instanceName":"72"}),makeQuery(id+"F2.opPattern","COPY",FACE,{"derivedFrom":subQ1,"instanceName":"73"}),makeQuery(id+"F2.opPattern","COPY",FACE,{"derivedFrom":subQ1,"instanceName":"74"}),makeQuery(id+"F2.opPattern","COPY",FACE,{"derivedFrom":subQ1,"instanceName":"75"}),makeQuery(id+"F2.opPattern","COPY",FACE,{"derivedFrom":subQ1,"instanceName":"76"}),makeQuery(id+"F2.opPattern","COPY",FACE,{"derivedFrom":subQ1,"instanceName":"77"}),makeQuery(id+"F2.opPattern","COPY",FACE,{"derivedFrom":subQ1,"instanceName":"78"}),makeQuery(id+"F2.opPattern","COPY",FACE,{"derivedFrom":subQ1,"instanceName":"79"}),makeQuery(id+"F2.opPattern","COPY",FACE,{"derivedFrom":subQ1,"instanceName":"80"}),makeQuery(id+"F2.opPattern","COPY",FACE,{"derivedFrom":subQ1,"instanceName":"81"}),makeQuery(id+"F2.opPattern","COPY",FACE,{"derivedFrom":subQ1,"instanceName":"82"}),makeQuery(id+"F2.opPattern","COPY",FACE,{"derivedFrom":subQ1,"instanceName":"83"}),makeQuery(id+"F2.opPattern","COPY",FACE,{"derivedFrom":subQ1,"instanceName":"84"}),makeQuery(id+"F2.opPattern","COPY",FACE,{"derivedFrom":subQ1,"instanceName":"85"}),makeQuery(id+"F2.opPattern","COPY",FACE,{"derivedFrom":subQ1,"instanceName":"86"}),makeQuery(id+"F2.opPattern","COPY",FACE,{"derivedFrom":subQ1,"instanceName":"87"}),makeQuery(id+"F2.opPattern","COPY",FACE,{"derivedFrom":subQ1,"instanceName":"88"}),makeQuery(id+"F2.opPattern","COPY",FACE,{"derivedFrom":subQ1,"instanceName":"89"}),makeQuery(id+"F2.opPattern","COPY",FACE,{"derivedFrom":subQ1,"instanceName":"90"}),makeQuery(id+"F2.opPattern","COPY",FACE,{"derivedFrom":subQ1,"instanceName":"91"}),makeQuery(id+"F2.opPattern","COPY",FACE,{"derivedFrom":subQ1,"instanceName":"92"}),makeQuery(id+"F2.opPattern","COPY",FACE,{"derivedFrom":subQ1,"instanceName":"93"}),makeQuery(id+"F2.opPattern","COPY",FACE,{"derivedFrom":subQ1,"instanceName":"94"}),makeQuery(id+"F2.opPattern","COPY",FACE,{"derivedFrom":subQ1,"instanceName":"95"}),makeQuery(id+"F3.opExtrude","CAP_FACE",FACE,{"disambiguationData":[OSD([subQ0])],"isStart":false})]});}
            var sketch = newSketch(context, id + "F12", { "sketchPlane" : qUnion([Q0])});
            skCircle(sketch, "E67.0", {"center": v(0, 0) * mm, "radius": 0.68 * mm});
            skCircle(sketch, "E68", {"center": v(0, 0) * mm, "radius": 1.6 * mm});
            skSolve(sketch);
        }
        {
            var Q0;
            Q0=qSketchRegion(id+"F12",true);
            var Q1;
            {var subQ0=sQuery(id+"F0.wireOp",EDGE,"E0");var subQ1=makeQuery(id+"F1.opExtrude","CAP_FACE",FACE,{"disambiguationData":[OSD([subQ0,sQuery(id+"F0.wireOp",EDGE,"E8"),sQuery(id+"F0.wireOp",EDGE,"E9"),sQuery(id+"F0.wireOp",EDGE,"E12"),sQuery(id+"F0.wireOp",EDGE,"E14")])],"isStart":true});Q1=makeQuery(id+"F4.opBoolean","MERGE",FACE,{"derivedFrom":[subQ1,makeQuery(id+"F2.opPattern","COPY",FACE,{"derivedFrom":subQ1,"instanceName":"1"}),makeQuery(id+"F2.opPattern","COPY",FACE,{"derivedFrom":subQ1,"instanceName":"2"}),makeQuery(id+"F2.opPattern","COPY",FACE,{"derivedFrom":subQ1,"instanceName":"3"}),makeQuery(id+"F2.opPattern","COPY",FACE,{"derivedFrom":subQ1,"instanceName":"4"}),makeQuery(id+"F2.opPattern","COPY",FACE,{"derivedFrom":subQ1,"instanceName":"5"}),makeQuery(id+"F2.opPattern","COPY",FACE,{"derivedFrom":subQ1,"instanceName":"6"}),makeQuery(id+"F2.opPattern","COPY",FACE,{"derivedFrom":subQ1,"instanceName":"7"}),makeQuery(id+"F2.opPattern","COPY",FACE,{"derivedFrom":subQ1,"instanceName":"8"}),makeQuery(id+"F2.opPattern","COPY",FACE,{"derivedFrom":subQ1,"instanceName":"9"}),makeQuery(id+"F2.opPattern","COPY",FACE,{"derivedFrom":subQ1,"instanceName":"10"}),makeQuery(id+"F2.opPattern","COPY",FACE,{"derivedFrom":subQ1,"instanceName":"11"}),makeQuery(id+"F2.opPattern","COPY",FACE,{"derivedFrom":subQ1,"instanceName":"12"}),makeQuery(id+"F2.opPattern","COPY",FACE,{"derivedFrom":subQ1,"instanceName":"13"}),makeQuery(id+"F2.opPattern","COPY",FACE,{"derivedFrom":subQ1,"instanceName":"14"}),makeQuery(id+"F2.opPattern","COPY",FACE,{"derivedFrom":subQ1,"instanceName":"15"}),makeQuery(id+"F2.opPattern","COPY",FACE,{"derivedFrom":subQ1,"instanceName":"16"}),makeQuery(id+"F2.opPattern","COPY",FACE,{"derivedFrom":subQ1,"instanceName":"17"}),makeQuery(id+"F2.opPattern","COPY",FACE,{"derivedFrom":subQ1,"instanceName":"18"}),makeQuery(id+"F2.opPattern","COPY",FACE,{"derivedFrom":subQ1,"instanceName":"19"}),makeQuery(id+"F2.opPattern","COPY",FACE,{"derivedFrom":subQ1,"instanceName":"20"}),makeQuery(id+"F2.opPattern","COPY",FACE,{"derivedFrom":subQ1,"instanceName":"21"}),makeQuery(id+"F2.opPattern","COPY",FACE,{"derivedFrom":subQ1,"instanceName":"22"}),makeQuery(id+"F2.opPattern","COPY",FACE,{"derivedFrom":subQ1,"instanceName":"23"}),makeQuery(id+"F2.opPattern","COPY",FACE,{"derivedFrom":subQ1,"instanceName":"24"}),makeQuery(id+"F2.opPattern","COPY",FACE,{"derivedFrom":subQ1,"instanceName":"25"}),makeQuery(id+"F2.opPattern","COPY",FACE,{"derivedFrom":subQ1,"instanceName":"26"}),makeQuery(id+"F2.opPattern","COPY",FACE,{"derivedFrom":subQ1,"instanceName":"27"}),makeQuery(id+"F2.opPattern","COPY",FACE,{"derivedFrom":subQ1,"instanceName":"28"}),makeQuery(id+"F2.opPattern","COPY",FACE,{"derivedFrom":subQ1,"instanceName":"29"}),makeQuery(id+"F2.opPattern","COPY",FACE,{"derivedFrom":subQ1,"instanceName":"30"}),makeQuery(id+"F2.opPattern","COPY",FACE,{"derivedFrom":subQ1,"instanceName":"31"}),makeQuery(id+"F2.opPattern","COPY",FACE,{"derivedFrom":subQ1,"instanceName":"32"}),makeQuery(id+"F2.opPattern","COPY",FACE,{"derivedFrom":subQ1,"instanceName":"33"}),makeQuery(id+"F2.opPattern","COPY",FACE,{"derivedFrom":subQ1,"instanceName":"34"}),makeQuery(id+"F2.opPattern","COPY",FACE,{"derivedFrom":subQ1,"instanceName":"35"}),makeQuery(id+"F2.opPattern","COPY",FACE,{"derivedFrom":subQ1,"instanceName":"36"}),makeQuery(id+"F2.opPattern","COPY",FACE,{"derivedFrom":subQ1,"instanceName":"37"}),makeQuery(id+"F2.opPattern","COPY",FACE,{"derivedFrom":subQ1,"instanceName":"38"}),makeQuery(id+"F2.opPattern","COPY",FACE,{"derivedFrom":subQ1,"instanceName":"39"}),makeQuery(id+"F2.opPattern","COPY",FACE,{"derivedFrom":subQ1,"instanceName":"40"}),makeQuery(id+"F2.opPattern","COPY",FACE,{"derivedFrom":subQ1,"instanceName":"41"}),makeQuery(id+"F2.opPattern","COPY",FACE,{"derivedFrom":subQ1,"instanceName":"42"}),makeQuery(id+"F2.opPattern","COPY",FACE,{"derivedFrom":subQ1,"instanceName":"43"}),makeQuery(id+"F2.opPattern","COPY",FACE,{"derivedFrom":subQ1,"instanceName":"44"}),makeQuery(id+"F2.opPattern","COPY",FACE,{"derivedFrom":subQ1,"instanceName":"45"}),makeQuery(id+"F2.opPattern","COPY",FACE,{"derivedFrom":subQ1,"instanceName":"46"}),makeQuery(id+"F2.opPattern","COPY",FACE,{"derivedFrom":subQ1,"instanceName":"47"}),makeQuery(id+"F2.opPattern","COPY",FACE,{"derivedFrom":subQ1,"instanceName":"48"}),makeQuery(id+"F2.opPattern","COPY",FACE,{"derivedFrom":subQ1,"instanceName":"49"}),makeQuery(id+"F2.opPattern","COPY",FACE,{"derivedFrom":subQ1,"instanceName":"50"}),makeQuery(id+"F2.opPattern","COPY",FACE,{"derivedFrom":subQ1,"instanceName":"51"}),makeQuery(id+"F2.opPattern","COPY",FACE,{"derivedFrom":subQ1,"instanceName":"52"}),makeQuery(id+"F2.opPattern","COPY",FACE,{"derivedFrom":subQ1,"instanceName":"53"}),makeQuery(id+"F2.opPattern","COPY",FACE,{"derivedFrom":subQ1,"instanceName":"54"}),makeQuery(id+"F2.opPattern","COPY",FACE,{"derivedFrom":subQ1,"instanceName":"55"}),makeQuery(id+"F2.opPattern","COPY",FACE,{"derivedFrom":subQ1,"instanceName":"56"}),makeQuery(id+"F2.opPattern","COPY",FACE,{"derivedFrom":subQ1,"instanceName":"57"}),makeQuery(id+"F2.opPattern","COPY",FACE,{"derivedFrom":subQ1,"instanceName":"58"}),makeQuery(id+"F2.opPattern","COPY",FACE,{"derivedFrom":subQ1,"instanceName":"59"}),makeQuery(id+"F2.opPattern","COPY",FACE,{"derivedFrom":subQ1,"instanceName":"60"}),makeQuery(id+"F2.opPattern","COPY",FACE,{"derivedFrom":subQ1,"instanceName":"61"}),makeQuery(id+"F2.opPattern","COPY",FACE,{"derivedFrom":subQ1,"instanceName":"62"}),makeQuery(id+"F2.opPattern","COPY",FACE,{"derivedFrom":subQ1,"instanceName":"63"}),makeQuery(id+"F2.opPattern","COPY",FACE,{"derivedFrom":subQ1,"instanceName":"64"}),makeQuery(id+"F2.opPattern","COPY",FACE,{"derivedFrom":subQ1,"instanceName":"65"}),makeQuery(id+"F2.opPattern","COPY",FACE,{"derivedFrom":subQ1,"instanceName":"66"}),makeQuery(id+"F2.opPattern","COPY",FACE,{"derivedFrom":subQ1,"instanceName":"67"}),makeQuery(id+"F2.opPattern","COPY",FACE,{"derivedFrom":subQ1,"instanceName":"68"}),makeQuery(id+"F2.opPattern","COPY",FACE,{"derivedFrom":subQ1,"instanceName":"69"}),makeQuery(id+"F2.opPattern","COPY",FACE,{"derivedFrom":subQ1,"instanceName":"70"}),makeQuery(id+"F2.opPattern","COPY",FACE,{"derivedFrom":subQ1,"instanceName":"71"}),makeQuery(id+"F2.opPattern","COPY",FACE,{"derivedFrom":subQ1,"instanceName":"72"}),makeQuery(id+"F2.opPattern","COPY",FACE,{"derivedFrom":subQ1,"instanceName":"73"}),makeQuery(id+"F2.opPattern","COPY",FACE,{"derivedFrom":subQ1,"instanceName":"74"}),makeQuery(id+"F2.opPattern","COPY",FACE,{"derivedFrom":subQ1,"instanceName":"75"}),makeQuery(id+"F2.opPattern","COPY",FACE,{"derivedFrom":subQ1,"instanceName":"76"}),makeQuery(id+"F2.opPattern","COPY",FACE,{"derivedFrom":subQ1,"instanceName":"77"}),makeQuery(id+"F2.opPattern","COPY",FACE,{"derivedFrom":subQ1,"instanceName":"78"}),makeQuery(id+"F2.opPattern","COPY",FACE,{"derivedFrom":subQ1,"instanceName":"79"}),makeQuery(id+"F2.opPattern","COPY",FACE,{"derivedFrom":subQ1,"instanceName":"80"}),makeQuery(id+"F2.opPattern","COPY",FACE,{"derivedFrom":subQ1,"instanceName":"81"}),makeQuery(id+"F2.opPattern","COPY",FACE,{"derivedFrom":subQ1,"instanceName":"82"}),makeQuery(id+"F2.opPattern","COPY",FACE,{"derivedFrom":subQ1,"instanceName":"83"}),makeQuery(id+"F2.opPattern","COPY",FACE,{"derivedFrom":subQ1,"instanceName":"84"}),makeQuery(id+"F2.opPattern","COPY",FACE,{"derivedFrom":subQ1,"instanceName":"85"}),makeQuery(id+"F2.opPattern","COPY",FACE,{"derivedFrom":subQ1,"instanceName":"86"}),makeQuery(id+"F2.opPattern","COPY",FACE,{"derivedFrom":subQ1,"instanceName":"87"}),makeQuery(id+"F2.opPattern","COPY",FACE,{"derivedFrom":subQ1,"instanceName":"88"}),makeQuery(id+"F2.opPattern","COPY",FACE,{"derivedFrom":subQ1,"instanceName":"89"}),makeQuery(id+"F2.opPattern","COPY",FACE,{"derivedFrom":subQ1,"instanceName":"90"}),makeQuery(id+"F2.opPattern","COPY",FACE,{"derivedFrom":subQ1,"instanceName":"91"}),makeQuery(id+"F2.opPattern","COPY",FACE,{"derivedFrom":subQ1,"instanceName":"92"}),makeQuery(id+"F2.opPattern","COPY",FACE,{"derivedFrom":subQ1,"instanceName":"93"}),makeQuery(id+"F2.opPattern","COPY",FACE,{"derivedFrom":subQ1,"instanceName":"94"}),makeQuery(id+"F2.opPattern","COPY",FACE,{"derivedFrom":subQ1,"instanceName":"95"}),makeQuery(id+"F3.opExtrude","CAP_FACE",FACE,{"disambiguationData":[OSD([subQ0])],"isStart":true})]});}
            extrude(context, id + "F13", {"entities" : qUnion([Q0]), "operationType" : NewBodyOperationType.REMOVE, "endBound" : BoundingType.UP_TO_SURFACE, "oppositeDirection" : true, "endBoundEntityFace" : qUnion([Q1]), "depth" : 25 * mm});
        }
        {
            var Q0;
            {var subQ0=sQuery(id+"F7.wireOp",EDGE,"E66");var subQ1=makeQuery(id+"F8.opExtrude","CAP_FACE",FACE,{"disambiguationData":[OSD([sQuery(id+"F7.wireOp",EDGE,"E59"),sQuery(id+"F7.wireOp",EDGE,"E60"),sQuery(id+"F7.wireOp",EDGE,"E64"),sQuery(id+"F7.wireOp",EDGE,"E65"),subQ0])],"isStart":true});Q0=makeQuery(id+"F11.opBoolean","MERGE",FACE,{"derivedFrom":[subQ1,makeQuery(id+"F9.opPattern","COPY",FACE,{"derivedFrom":subQ1,"instanceName":"1"}),makeQuery(id+"F9.opPattern","COPY",FACE,{"derivedFrom":subQ1,"instanceName":"2"}),makeQuery(id+"F9.opPattern","COPY",FACE,{"derivedFrom":subQ1,"instanceName":"3"}),makeQuery(id+"F9.opPattern","COPY",FACE,{"derivedFrom":subQ1,"instanceName":"4"}),makeQuery(id+"F9.opPattern","COPY",FACE,{"derivedFrom":subQ1,"instanceName":"5"}),makeQuery(id+"F9.opPattern","COPY",FACE,{"derivedFrom":subQ1,"instanceName":"6"}),makeQuery(id+"F9.opPattern","COPY",FACE,{"derivedFrom":subQ1,"instanceName":"7"}),makeQuery(id+"F9.opPattern","COPY",FACE,{"derivedFrom":subQ1,"instanceName":"8"}),makeQuery(id+"F9.opPattern","COPY",FACE,{"derivedFrom":subQ1,"instanceName":"9"}),makeQuery(id+"F9.opPattern","COPY",FACE,{"derivedFrom":subQ1,"instanceName":"10"}),makeQuery(id+"F9.opPattern","COPY",FACE,{"derivedFrom":subQ1,"instanceName":"11"}),makeQuery(id+"F10.opExtrude","CAP_FACE",FACE,{"disambiguationData":[OSD([subQ0])],"isStart":true})]});}
            var sketch = newSketch(context, id + "F14", { "sketchPlane" : qUnion([Q0])});
            skCircle(sketch, "E69", {"center": v(0, 0) * mm, "radius": 0.25 * mm});
            skSolve(sketch);
        }
        {
            var Q0;
            Q0=qSketchRegion(id+"F14",true);
            extrude(context, id + "F15", {"entities" : qUnion([Q0]), "operationType" : NewBodyOperationType.ADD, "depth" : 0.35 * mm});
        }
        {
            var Q0;
            Q0=makeQuery(id+"F15.opExtrude","CAP_FACE",FACE,{"disambiguationData":[OSD([sQuery(id+"F14.wireOp",EDGE,"E69")])],"isStart":false});
            var sketch = newSketch(context, id + "F16", { "sketchPlane" : qUnion([Q0])});
            skCircle(sketch, "E70", {"center": v(0, 0) * mm, "radius": 0.1 * mm});
            skSolve(sketch);
        }
        {
            var Q0;
            Q0=qSketchRegion(id+"F16",true);
            extrude(context, id + "F17", {"entities" : qUnion([Q0]), "operationType" : NewBodyOperationType.ADD, "depth" : 0.5 * mm});
        }
    });
